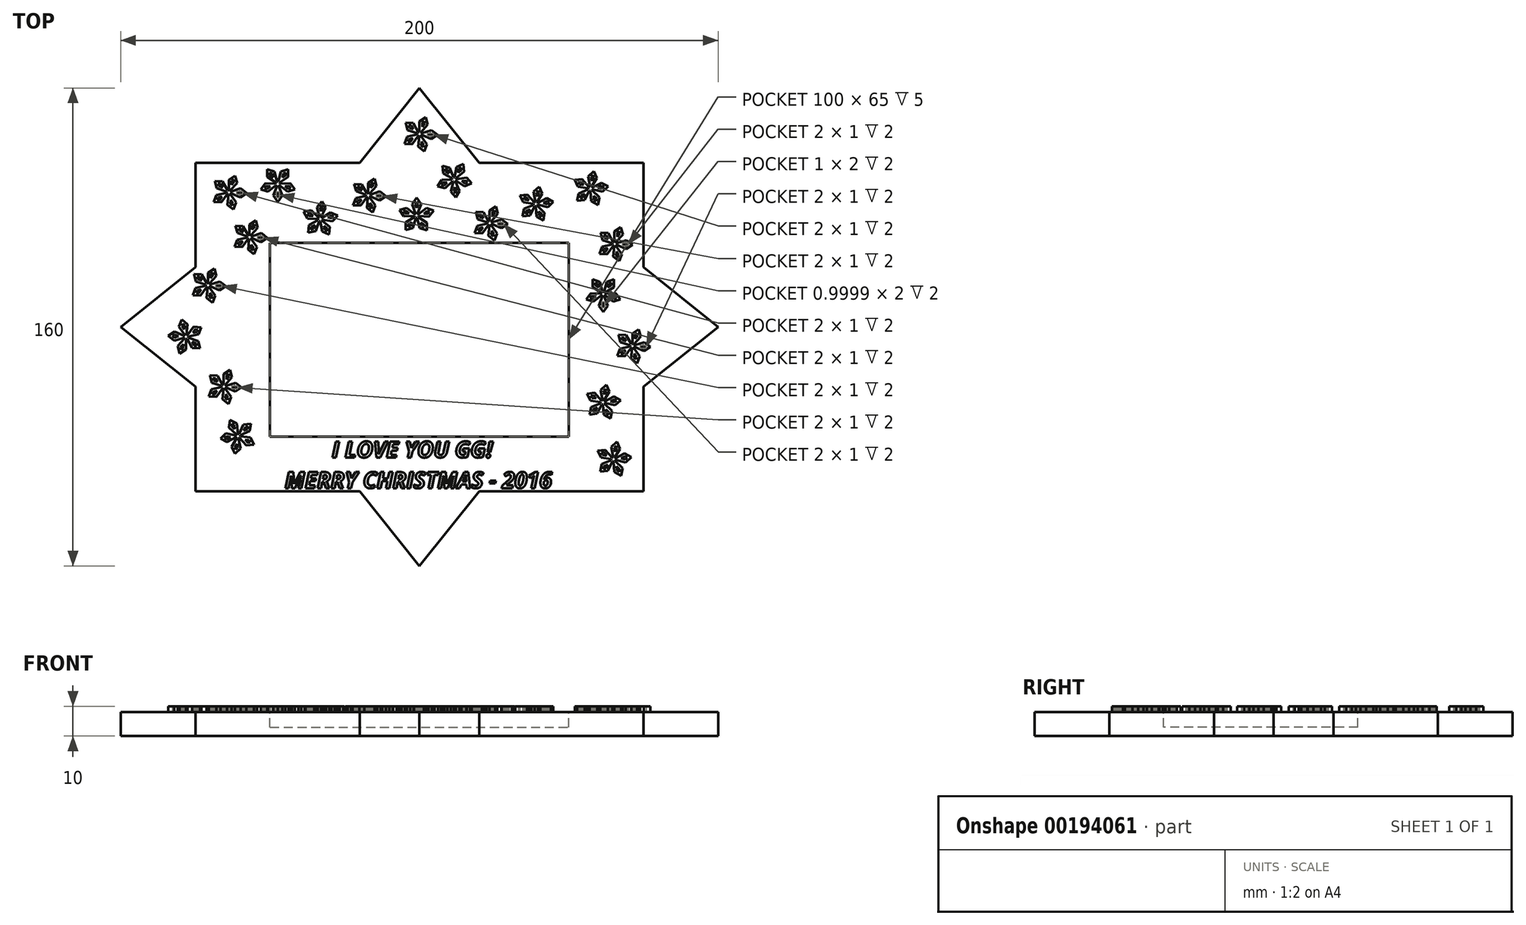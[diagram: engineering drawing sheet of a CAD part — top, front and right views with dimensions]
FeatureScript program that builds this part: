
annotation { "Feature Type Name" : "Feature", "Feature Type Description" : "" }
export const myFeature = defineFeature(function(context is Context, id is Id, definition is map)
    precondition{}
    {
        {
            var Q0;
            Q0=qCreatedBy(makeId("Top.planeOp"),FACE);
            var sketch = newSketch(context, id + "F0", { "sketchPlane" : qUnion([Q0])});
            skLineSegment(sketch, "E0.bottom", {"start": v(75, 55) * mm, "end": v(20, 55) * mm});
            skLineSegment(sketch, "E0.top", {"start": v(75, -55) * mm, "end": v(20, -55) * mm});
            skLineSegment(sketch, "E0.left", {"start": v(75, 55) * mm, "end": v(75, 20) * mm});
            skLineSegment(sketch, "E0.right", {"start": v(-75, 55) * mm, "end": v(-75, 20) * mm});
            skLineSegment(sketch, "E1", {"start": v(75, 20) * mm, "end": v(100, 0) * mm});
            skLineSegment(sketch, "E2", {"start": v(-20, 55) * mm, "end": v(0, 80) * mm});
            skLineSegment(sketch, "E3", {"start": v(0, 80) * mm, "end": v(20, 55) * mm});
            skLineSegment(sketch, "E4.MirrorCS", {"start": v(-20, -55) * mm, "end": v(0, -80) * mm});
            skLineSegment(sketch, "E5.MirrorCS", {"start": v(0, -80) * mm, "end": v(20, -55) * mm});
            skLineSegment(sketch, "E6.MirrorCS", {"start": v(75, -20) * mm, "end": v(100, 0) * mm});
            skLineSegment(sketch, "E7.MirrorCS", {"start": v(-75, 20) * mm, "end": v(-100, 0) * mm});
            skLineSegment(sketch, "E8.MirrorCS", {"start": v(-75, -20) * mm, "end": v(-100, 0) * mm});
            skLineSegment(sketch, "E9.trimOffspring", {"start": v(-75, -20) * mm, "end": v(-75, -55) * mm});
            skLineSegment(sketch, "E10.trimOffspring", {"start": v(75, -20) * mm, "end": v(75, -55) * mm});
            skLineSegment(sketch, "E11.trimOffspring", {"start": v(-20, -55) * mm, "end": v(-75, -55) * mm});
            skLineSegment(sketch, "E12.trimOffspring", {"start": v(-20, 55) * mm, "end": v(-75, 55) * mm});
            skPoint(sketch, "E13.MirrorCS.end.orphan", {"position": v(75, 34.57) * mm});
            skPoint(sketch, "E13.MirrorCS.start.orphan", {"position": v(100, 0) * mm});
            skPoint(sketch, "E14.orphan", {"position": v(75, -34.57) * mm});
            skSolve(sketch);
        }
        {
            var Q0;
            Q0=qSketchRegion(id+"F0",true);
            extrude(context, id + "F1", {"entities" : qUnion([Q0]), "endBound" : BoundingType.SYMMETRIC, "depth" : 8 * mm});
        }
        {
            var Q0;
            Q0=makeQuery(id+"F1.opExtrude","CAP_FACE",FACE,{"disambiguationData":[OSD([sQuery(id+"F0.wireOp",EDGE,"E0.bottom"),sQuery(id+"F0.wireOp",EDGE,"E0.top"),sQuery(id+"F0.wireOp",EDGE,"E0.left"),sQuery(id+"F0.wireOp",EDGE,"E0.right"),sQuery(id+"F0.wireOp",EDGE,"b7ca5f3b-2874-41bd-b902-1c79f96a0a8620.MirrorC"),sQuery(id+"F0.wireOp",EDGE,"b7ca5f3b-2874-41bd-b902-1c79f96a0a8621.MirrorC"),sQuery(id+"F0.wireOp",EDGE,"b7ca5f3b-2874-41bd-b902-1c79f96a0a8622.MirrorCS"),sQuery(id+"F0.wireOp",EDGE,"b7ca5f3b-2874-41bd-b902-1c79f96a0a8623.MirrorCS"),sQuery(id+"F0.wireOp",EDGE,"b7ca5f3b-2874-41bd-b902-1c79f96a0a8624.MirrorCS"),sQuery(id+"F0.wireOp",EDGE,"b7ca5f3b-2874-41bd-b902-1c79f96a0a8625.MirrorCS"),sQuery(id+"F0.wireOp",EDGE,"70034771-ba44-435e-ab74-29499f25fa1546.MirrorC"),sQuery(id+"F0.wireOp",EDGE,"70034771-ba44-435e-ab74-29499f25fa1547.MirrorCS"),sQuery(id+"F0.wireOp",EDGE,"70034771-ba44-435e-ab74-29499f25fa1548.MirrorC"),sQuery(id+"F0.wireOp",EDGE,"70034771-ba44-435e-ab74-29499f25fa1549.MirrorCS"),sQuery(id+"F0.wireOp",EDGE,"70034771-ba44-435e-ab74-29499f25fa1550.MirrorCS"),sQuery(id+"F0.wireOp",EDGE,"70034771-ba44-435e-ab74-29499f25fa1551.MirrorCS"),sQuery(id+"F0.wireOp",EDGE,"E1"),sQuery(id+"F0.wireOp",EDGE,"E2"),sQuery(id+"F0.wireOp",EDGE,"E3"),sQuery(id+"F0.wireOp",EDGE,"E4.MirrorCS"),sQuery(id+"F0.wireOp",EDGE,"E5.MirrorCS"),sQuery(id+"F0.wireOp",EDGE,"E6.MirrorCS"),sQuery(id+"F0.wireOp",EDGE,"E7.MirrorCS"),sQuery(id+"F0.wireOp",EDGE,"E8.MirrorCS"),sQuery(id+"F0.wireOp",EDGE,"E9.trimOffspring"),sQuery(id+"F0.wireOp",EDGE,"E10.trimOffspring"),sQuery(id+"F0.wireOp",EDGE,"E11.trimOffspring"),sQuery(id+"F0.wireOp",EDGE,"E12.trimOffspring")])],"isStart":false});
            var sketch = newSketch(context, id + "F2", { "sketchPlane" : qUnion([Q0])});
            skCircle(sketch, "E15.cCircle", {"center": v(65.31, 27.78) * mm, "radius": 6 * mm, "construction": true});
            skLineSegment(sketch, "E15.0", {"start": v(71.3, 27.48) * mm, "end": v(66.88, 22) * mm, "construction": true});
            skLineSegment(sketch, "E15.1", {"start": v(66.88, 22) * mm, "end": v(60.29, 24.5) * mm, "construction": true});
            skLineSegment(sketch, "E15.2", {"start": v(60.29, 24.5) * mm, "end": v(60.64, 31.55) * mm, "construction": true});
            skLineSegment(sketch, "E15.3", {"start": v(60.64, 31.55) * mm, "end": v(67.45, 33.39) * mm, "construction": true});
            skLineSegment(sketch, "E15.4", {"start": v(67.45, 33.39) * mm, "end": v(71.3, 27.48) * mm, "construction": true});
            skLineSegment(sketch, "E16", {"start": v(60.64, 31.55) * mm, "end": v(61.32, 29.08) * mm});
            skLineSegment(sketch, "E17", {"start": v(61.32, 29.08) * mm, "end": v(64.6, 28.02) * mm});
            skLineSegment(sketch, "E18", {"start": v(64.94, 28.43) * mm, "end": v(63.2, 31.42) * mm});
            skLineSegment(sketch, "E19", {"start": v(63.2, 31.42) * mm, "end": v(60.64, 31.55) * mm});
            skLineSegment(sketch, "E20", {"start": v(60.29, 24.5) * mm, "end": v(62.84, 24.38) * mm});
            skLineSegment(sketch, "E21", {"start": v(62.84, 24.38) * mm, "end": v(64.87, 27.18) * mm});
            skLineSegment(sketch, "E22", {"start": v(64.58, 27.63) * mm, "end": v(61.2, 26.9) * mm});
            skLineSegment(sketch, "E23", {"start": v(61.2, 26.9) * mm, "end": v(60.29, 24.5) * mm});
            skLineSegment(sketch, "E24", {"start": v(66.88, 22) * mm, "end": v(67.78, 24.38) * mm});
            skLineSegment(sketch, "E25", {"start": v(67.78, 24.38) * mm, "end": v(65.75, 27.18) * mm});
            skLineSegment(sketch, "E26", {"start": v(65.24, 27.04) * mm, "end": v(64.89, 23.6) * mm});
            skLineSegment(sketch, "E27", {"start": v(64.89, 23.6) * mm, "end": v(66.88, 22) * mm});
            skLineSegment(sketch, "E28", {"start": v(66, 27.48) * mm, "end": v(69.16, 26.09) * mm});
            skLineSegment(sketch, "E29", {"start": v(69.16, 26.09) * mm, "end": v(71.3, 27.48) * mm});
            skLineSegment(sketch, "E30", {"start": v(66.03, 28.02) * mm, "end": v(69.31, 29.08) * mm});
            skLineSegment(sketch, "E31", {"start": v(69.31, 29.08) * mm, "end": v(71.3, 27.48) * mm});
            skLineSegment(sketch, "E32", {"start": v(67.45, 33.39) * mm, "end": v(68.12, 30.92) * mm});
            skLineSegment(sketch, "E33", {"start": v(68.12, 30.92) * mm, "end": v(65.81, 28.34) * mm});
            skLineSegment(sketch, "E34", {"start": v(65.31, 28.53) * mm, "end": v(65.31, 31.99) * mm});
            skLineSegment(sketch, "E35", {"start": v(65.31, 31.99) * mm, "end": v(67.45, 33.39) * mm});
            skLineSegment(sketch, "E36", {"start": v(69.38, 30.43) * mm, "end": v(69.1, 24.74) * mm, "construction": true});
            skLineSegment(sketch, "E37", {"start": v(69.1, 24.74) * mm, "end": v(63.58, 23.25) * mm, "construction": true});
            skLineSegment(sketch, "E38", {"start": v(63.58, 23.25) * mm, "end": v(60.47, 28.03) * mm, "construction": true});
            skLineSegment(sketch, "E39", {"start": v(60.47, 28.03) * mm, "end": v(64.05, 32.47) * mm, "construction": true});
            skLineSegment(sketch, "E40", {"start": v(64.05, 32.47) * mm, "end": v(69.38, 30.43) * mm, "construction": true});
            skLineSegment(sketch, "E41", {"start": v(67.45, 33.39) * mm, "end": v(65.31, 27.78) * mm, "construction": true});
            skLineSegment(sketch, "E42", {"start": v(71.3, 27.48) * mm, "end": v(65.31, 27.78) * mm, "construction": true});
            skLineSegment(sketch, "E43", {"start": v(66.88, 22) * mm, "end": v(65.31, 27.78) * mm, "construction": true});
            skLineSegment(sketch, "E44", {"start": v(60.29, 24.5) * mm, "end": v(65.31, 27.78) * mm, "construction": true});
            skLineSegment(sketch, "E45", {"start": v(60.64, 31.55) * mm, "end": v(65.31, 27.78) * mm, "construction": true});
            skArc(sketch, "E46", {"start": v(64.87, 27.18) * mm, "mid": v(65.05, 27.08) * mm, "end": v(65.24, 27.04) * mm});
            skArc(sketch, "E47.trimOffspring", {"start": v(64.6, 28.02) * mm, "mid": v(64.56, 27.82) * mm, "end": v(64.58, 27.63) * mm});
            skArc(sketch, "E48.trimOffspring", {"start": v(65.31, 28.53) * mm, "mid": v(65.12, 28.5) * mm, "end": v(64.94, 28.43) * mm});
            skArc(sketch, "E49.trimOffspring", {"start": v(66.03, 28.02) * mm, "mid": v(65.94, 28.2) * mm, "end": v(65.81, 28.34) * mm});
            skArc(sketch, "E50.trimOffspring", {"start": v(65.75, 27.18) * mm, "mid": v(65.9, 27.31) * mm, "end": v(66, 27.48) * mm});
            skLineSegment(sketch, "E51", {"start": v(61.72, 30.68) * mm, "end": v(61.94, 29.86) * mm});
            skLineSegment(sketch, "E52", {"start": v(61.94, 29.86) * mm, "end": v(63.28, 29.43) * mm});
            skLineSegment(sketch, "E53", {"start": v(63.28, 29.43) * mm, "end": v(62.57, 30.64) * mm});
            skLineSegment(sketch, "E54", {"start": v(62.57, 30.64) * mm, "end": v(61.72, 30.68) * mm});
            skLineSegment(sketch, "E55", {"start": v(66.96, 32.1) * mm, "end": v(67.18, 31.27) * mm});
            skLineSegment(sketch, "E56", {"start": v(67.18, 31.27) * mm, "end": v(66.25, 30.23) * mm});
            skLineSegment(sketch, "E57", {"start": v(66.25, 30.23) * mm, "end": v(66.25, 31.63) * mm});
            skLineSegment(sketch, "E58", {"start": v(66.25, 31.63) * mm, "end": v(66.96, 32.1) * mm});
            skLineSegment(sketch, "E59", {"start": v(66.52, 23.33) * mm, "end": v(66.82, 24.12) * mm});
            skLineSegment(sketch, "E60", {"start": v(66.82, 24.12) * mm, "end": v(66, 25.26) * mm});
            skLineSegment(sketch, "E61", {"start": v(66, 25.26) * mm, "end": v(65.85, 23.86) * mm});
            skLineSegment(sketch, "E62", {"start": v(65.85, 23.86) * mm, "end": v(66.52, 23.33) * mm});
            skLineSegment(sketch, "E63", {"start": v(69.93, 27.55) * mm, "end": v(69.26, 28.09) * mm});
            skLineSegment(sketch, "E64", {"start": v(69.26, 28.09) * mm, "end": v(67.93, 27.65) * mm});
            skLineSegment(sketch, "E65", {"start": v(67.93, 27.65) * mm, "end": v(69.21, 27.09) * mm});
            skLineSegment(sketch, "E66", {"start": v(69.21, 27.09) * mm, "end": v(69.93, 27.55) * mm});
            skLineSegment(sketch, "E67", {"start": v(61.44, 25.26) * mm, "end": v(62.3, 25.22) * mm});
            skLineSegment(sketch, "E68", {"start": v(62.3, 25.22) * mm, "end": v(63.12, 26.35) * mm});
            skLineSegment(sketch, "E69", {"start": v(63.12, 26.35) * mm, "end": v(61.75, 26.06) * mm});
            skLineSegment(sketch, "E70", {"start": v(61.75, 26.06) * mm, "end": v(61.44, 25.26) * mm});
            skLineSegment(sketch, "E71", {"start": v(58.04, 15.9) * mm, "end": v(58.05, 13.34) * mm});
            skLineSegment(sketch, "E72", {"start": v(58.05, 13.34) * mm, "end": v(60.95, 11.46) * mm});
            skLineSegment(sketch, "E73", {"start": v(61.38, 11.77) * mm, "end": v(60.47, 15.1) * mm});
            skLineSegment(sketch, "E74", {"start": v(60.47, 15.1) * mm, "end": v(58.04, 15.9) * mm});
            skLineSegment(sketch, "E75", {"start": v(55.87, 9.19) * mm, "end": v(58.3, 8.4) * mm});
            skLineSegment(sketch, "E76", {"start": v(58.3, 8.4) * mm, "end": v(61, 10.58) * mm});
            skLineSegment(sketch, "E77", {"start": v(60.83, 11.09) * mm, "end": v(57.38, 11.26) * mm});
            skLineSegment(sketch, "E78", {"start": v(57.38, 11.26) * mm, "end": v(55.87, 9.19) * mm});
            skLineSegment(sketch, "E79", {"start": v(61.59, 5.05) * mm, "end": v(63.08, 7.13) * mm});
            skLineSegment(sketch, "E80", {"start": v(63.08, 7.13) * mm, "end": v(61.84, 10.35) * mm});
            skLineSegment(sketch, "E81", {"start": v(61.3, 10.35) * mm, "end": v(60.08, 7.12) * mm});
            skLineSegment(sketch, "E82", {"start": v(60.08, 7.12) * mm, "end": v(61.59, 5.05) * mm});
            skLineSegment(sketch, "E83", {"start": v(62.16, 10.58) * mm, "end": v(64.85, 8.42) * mm});
            skLineSegment(sketch, "E84", {"start": v(64.85, 8.42) * mm, "end": v(67.29, 9.2) * mm});
            skLineSegment(sketch, "E85", {"start": v(62.32, 11.09) * mm, "end": v(65.77, 11.27) * mm});
            skLineSegment(sketch, "E86", {"start": v(65.77, 11.27) * mm, "end": v(67.29, 9.2) * mm});
            skLineSegment(sketch, "E87", {"start": v(65.1, 15.9) * mm, "end": v(65.1, 13.35) * mm});
            skLineSegment(sketch, "E88", {"start": v(65.1, 13.35) * mm, "end": v(62.2, 11.46) * mm});
            skLineSegment(sketch, "E89", {"start": v(61.77, 11.77) * mm, "end": v(62.66, 15.11) * mm});
            skLineSegment(sketch, "E90", {"start": v(62.66, 15.11) * mm, "end": v(65.1, 15.9) * mm});
            skArc(sketch, "E91", {"start": v(61, 10.58) * mm, "mid": v(61.14, 10.44) * mm, "end": v(61.3, 10.35) * mm});
            skArc(sketch, "E92.trimOffspring", {"start": v(60.95, 11.46) * mm, "mid": v(60.86, 11.28) * mm, "end": v(60.83, 11.09) * mm});
            skArc(sketch, "E93.trimOffspring", {"start": v(61.77, 11.77) * mm, "mid": v(61.57, 11.8) * mm, "end": v(61.38, 11.77) * mm});
            skArc(sketch, "E94.trimOffspring", {"start": v(62.32, 11.09) * mm, "mid": v(62.29, 11.28) * mm, "end": v(62.2, 11.46) * mm});
            skArc(sketch, "E95.trimOffspring", {"start": v(61.84, 10.35) * mm, "mid": v(62.02, 10.44) * mm, "end": v(62.16, 10.58) * mm});
            skLineSegment(sketch, "E96", {"start": v(58.86, 14.78) * mm, "end": v(58.86, 13.93) * mm});
            skLineSegment(sketch, "E97", {"start": v(58.86, 13.93) * mm, "end": v(60.03, 13.17) * mm});
            skLineSegment(sketch, "E98", {"start": v(60.03, 13.17) * mm, "end": v(59.67, 14.52) * mm});
            skLineSegment(sketch, "E99", {"start": v(59.67, 14.52) * mm, "end": v(58.86, 14.78) * mm});
            skLineSegment(sketch, "E100", {"start": v(64.28, 14.8) * mm, "end": v(64.28, 13.94) * mm});
            skLineSegment(sketch, "E101", {"start": v(64.28, 13.94) * mm, "end": v(63.11, 13.17) * mm});
            skLineSegment(sketch, "E102", {"start": v(63.11, 13.17) * mm, "end": v(63.47, 14.52) * mm});
            skLineSegment(sketch, "E103", {"start": v(63.47, 14.52) * mm, "end": v(64.28, 14.8) * mm});
            skLineSegment(sketch, "E104", {"start": v(61.58, 6.43) * mm, "end": v(62.08, 7.12) * mm});
            skLineSegment(sketch, "E105", {"start": v(62.08, 7.12) * mm, "end": v(61.58, 8.43) * mm});
            skLineSegment(sketch, "E106", {"start": v(61.58, 8.43) * mm, "end": v(61.08, 7.12) * mm});
            skLineSegment(sketch, "E107", {"start": v(61.08, 7.12) * mm, "end": v(61.58, 6.43) * mm});
            skLineSegment(sketch, "E108", {"start": v(65.97, 9.63) * mm, "end": v(65.47, 10.32) * mm});
            skLineSegment(sketch, "E109", {"start": v(65.47, 10.32) * mm, "end": v(64.07, 10.25) * mm});
            skLineSegment(sketch, "E110", {"start": v(64.07, 10.25) * mm, "end": v(65.16, 9.37) * mm});
            skLineSegment(sketch, "E111", {"start": v(65.16, 9.37) * mm, "end": v(65.97, 9.63) * mm});
            skLineSegment(sketch, "E112", {"start": v(57.19, 9.62) * mm, "end": v(58, 9.35) * mm});
            skLineSegment(sketch, "E113", {"start": v(58, 9.35) * mm, "end": v(59.09, 10.24) * mm});
            skLineSegment(sketch, "E114", {"start": v(59.09, 10.24) * mm, "end": v(57.69, 10.3) * mm});
            skLineSegment(sketch, "E115", {"start": v(57.69, 10.3) * mm, "end": v(57.19, 9.62) * mm});
            skLineSegment(sketch, "E116", {"start": v(52, 49.2) * mm, "end": v(53.08, 46.88) * mm});
            skLineSegment(sketch, "E117", {"start": v(53.08, 46.88) * mm, "end": v(56.5, 46.4) * mm});
            skLineSegment(sketch, "E118", {"start": v(56.76, 46.87) * mm, "end": v(54.53, 49.5) * mm});
            skLineSegment(sketch, "E119", {"start": v(54.53, 49.5) * mm, "end": v(52, 49.2) * mm});
            skLineSegment(sketch, "E120", {"start": v(52.86, 42.2) * mm, "end": v(55.4, 42.52) * mm});
            skLineSegment(sketch, "E121", {"start": v(55.4, 42.52) * mm, "end": v(56.92, 45.62) * mm});
            skLineSegment(sketch, "E122", {"start": v(56.55, 46.01) * mm, "end": v(53.35, 44.7) * mm});
            skLineSegment(sketch, "E123", {"start": v(53.35, 44.7) * mm, "end": v(52.86, 42.2) * mm});
            skLineSegment(sketch, "E124", {"start": v(59.79, 40.86) * mm, "end": v(60.27, 43.37) * mm});
            skLineSegment(sketch, "E125", {"start": v(60.27, 43.37) * mm, "end": v(57.78, 45.77) * mm});
            skLineSegment(sketch, "E126", {"start": v(57.3, 45.55) * mm, "end": v(57.55, 42.1) * mm});
            skLineSegment(sketch, "E127", {"start": v(57.55, 42.1) * mm, "end": v(59.79, 40.86) * mm});
            skLineSegment(sketch, "E128", {"start": v(57.97, 46.12) * mm, "end": v(61.33, 45.3) * mm});
            skLineSegment(sketch, "E129", {"start": v(61.33, 45.3) * mm, "end": v(63.2, 47.04) * mm});
            skLineSegment(sketch, "E130", {"start": v(57.9, 46.65) * mm, "end": v(60.96, 48.27) * mm});
            skLineSegment(sketch, "E131", {"start": v(60.96, 48.27) * mm, "end": v(63.2, 47.04) * mm});
            skLineSegment(sketch, "E132", {"start": v(58.38, 52.19) * mm, "end": v(59.46, 49.87) * mm});
            skLineSegment(sketch, "E133", {"start": v(59.46, 49.87) * mm, "end": v(57.64, 46.93) * mm});
            skLineSegment(sketch, "E134", {"start": v(57.11, 47.03) * mm, "end": v(56.51, 50.43) * mm});
            skLineSegment(sketch, "E135", {"start": v(56.51, 50.43) * mm, "end": v(58.38, 52.19) * mm});
            skArc(sketch, "E136", {"start": v(56.92, 45.62) * mm, "mid": v(57.1, 45.56) * mm, "end": v(57.3, 45.55) * mm});
            skArc(sketch, "E137.trimOffspring", {"start": v(56.5, 46.4) * mm, "mid": v(56.5, 46.2) * mm, "end": v(56.55, 46.01) * mm});
            skArc(sketch, "E138.trimOffspring", {"start": v(57.11, 47.03) * mm, "mid": v(56.93, 46.97) * mm, "end": v(56.76, 46.87) * mm});
            skArc(sketch, "E139.trimOffspring", {"start": v(57.9, 46.65) * mm, "mid": v(57.8, 46.8) * mm, "end": v(57.64, 46.93) * mm});
            skArc(sketch, "E140.trimOffspring", {"start": v(57.78, 45.77) * mm, "mid": v(57.9, 45.93) * mm, "end": v(57.97, 46.12) * mm});
            skLineSegment(sketch, "E141", {"start": v(53.2, 48.53) * mm, "end": v(53.56, 47.76) * mm});
            skLineSegment(sketch, "E142", {"start": v(53.56, 47.76) * mm, "end": v(54.95, 47.56) * mm});
            skLineSegment(sketch, "E143", {"start": v(54.95, 47.56) * mm, "end": v(54.05, 48.63) * mm});
            skLineSegment(sketch, "E144", {"start": v(54.05, 48.63) * mm, "end": v(53.2, 48.53) * mm});
            skLineSegment(sketch, "E145", {"start": v(58.12, 50.83) * mm, "end": v(58.48, 50.06) * mm});
            skLineSegment(sketch, "E146", {"start": v(58.48, 50.06) * mm, "end": v(57.74, 48.87) * mm});
            skLineSegment(sketch, "E147", {"start": v(57.74, 48.87) * mm, "end": v(57.5, 50.25) * mm});
            skLineSegment(sketch, "E148", {"start": v(57.5, 50.25) * mm, "end": v(58.12, 50.83) * mm});
            skLineSegment(sketch, "E149", {"start": v(59.2, 42.11) * mm, "end": v(59.36, 42.95) * mm});
            skLineSegment(sketch, "E150", {"start": v(59.36, 42.95) * mm, "end": v(58.35, 43.92) * mm});
            skLineSegment(sketch, "E151", {"start": v(58.35, 43.92) * mm, "end": v(58.46, 42.53) * mm});
            skLineSegment(sketch, "E152", {"start": v(58.46, 42.53) * mm, "end": v(59.2, 42.11) * mm});
            skLineSegment(sketch, "E153", {"start": v(61.83, 46.87) * mm, "end": v(61.08, 47.28) * mm});
            skLineSegment(sketch, "E154", {"start": v(61.08, 47.28) * mm, "end": v(59.84, 46.62) * mm});
            skLineSegment(sketch, "E155", {"start": v(59.84, 46.62) * mm, "end": v(61.2, 46.28) * mm});
            skLineSegment(sketch, "E156", {"start": v(61.2, 46.28) * mm, "end": v(61.83, 46.87) * mm});
            skLineSegment(sketch, "E157", {"start": v(53.87, 43.14) * mm, "end": v(54.72, 43.25) * mm});
            skLineSegment(sketch, "E158", {"start": v(54.72, 43.25) * mm, "end": v(55.33, 44.5) * mm});
            skLineSegment(sketch, "E159", {"start": v(55.33, 44.5) * mm, "end": v(54.04, 43.98) * mm});
            skLineSegment(sketch, "E160", {"start": v(54.04, 43.98) * mm, "end": v(53.87, 43.14) * mm});
            skLineSegment(sketch, "E161", {"start": v(66.62, -2.64) * mm, "end": v(67.3, -5.1) * mm});
            skLineSegment(sketch, "E162", {"start": v(67.3, -5.1) * mm, "end": v(70.58, -6.18) * mm});
            skLineSegment(sketch, "E163", {"start": v(70.91, -5.76) * mm, "end": v(69.18, -2.77) * mm});
            skLineSegment(sketch, "E164", {"start": v(69.18, -2.77) * mm, "end": v(66.62, -2.64) * mm});
            skLineSegment(sketch, "E165", {"start": v(66.26, -9.68) * mm, "end": v(68.82, -9.8) * mm});
            skLineSegment(sketch, "E166", {"start": v(68.82, -9.8) * mm, "end": v(70.85, -7.02) * mm});
            skLineSegment(sketch, "E167", {"start": v(70.56, -6.57) * mm, "end": v(67.18, -7.3) * mm});
            skLineSegment(sketch, "E168", {"start": v(67.18, -7.3) * mm, "end": v(66.26, -9.68) * mm});
            skLineSegment(sketch, "E169", {"start": v(72.85, -12.2) * mm, "end": v(73.76, -9.8) * mm});
            skLineSegment(sketch, "E170", {"start": v(73.76, -9.8) * mm, "end": v(71.73, -7.02) * mm});
            skLineSegment(sketch, "E171", {"start": v(71.21, -7.15) * mm, "end": v(70.86, -10.6) * mm});
            skLineSegment(sketch, "E172", {"start": v(70.86, -10.6) * mm, "end": v(72.85, -12.2) * mm});
            skLineSegment(sketch, "E173", {"start": v(71.98, -6.71) * mm, "end": v(75.14, -8.1) * mm});
            skLineSegment(sketch, "E174", {"start": v(75.14, -8.1) * mm, "end": v(77.28, -6.71) * mm});
            skLineSegment(sketch, "E175", {"start": v(72, -6.18) * mm, "end": v(75.29, -5.1) * mm});
            skLineSegment(sketch, "E176", {"start": v(75.29, -5.1) * mm, "end": v(77.28, -6.71) * mm});
            skLineSegment(sketch, "E177", {"start": v(73.43, -0.8) * mm, "end": v(74.1, -3.28) * mm});
            skLineSegment(sketch, "E178", {"start": v(74.1, -3.28) * mm, "end": v(71.8, -5.85) * mm});
            skLineSegment(sketch, "E179", {"start": v(71.3, -5.66) * mm, "end": v(71.3, -2.2) * mm});
            skLineSegment(sketch, "E180", {"start": v(71.3, -2.2) * mm, "end": v(73.43, -0.8) * mm});
            skArc(sketch, "E181", {"start": v(70.85, -7.02) * mm, "mid": v(71.02, -7.1) * mm, "end": v(71.21, -7.15) * mm});
            skArc(sketch, "E182.trimOffspring", {"start": v(70.58, -6.18) * mm, "mid": v(70.54, -6.37) * mm, "end": v(70.56, -6.57) * mm});
            skArc(sketch, "E183.trimOffspring", {"start": v(71.3, -5.66) * mm, "mid": v(71.1, -5.68) * mm, "end": v(70.91, -5.76) * mm});
            skArc(sketch, "E184.trimOffspring", {"start": v(72, -6.18) * mm, "mid": v(71.92, -6) * mm, "end": v(71.8, -5.85) * mm});
            skArc(sketch, "E185.trimOffspring", {"start": v(71.73, -7.02) * mm, "mid": v(71.87, -6.88) * mm, "end": v(71.98, -6.71) * mm});
            skLineSegment(sketch, "E186", {"start": v(67.7, -3.5) * mm, "end": v(67.92, -4.33) * mm});
            skLineSegment(sketch, "E187", {"start": v(67.92, -4.33) * mm, "end": v(69.25, -4.76) * mm});
            skLineSegment(sketch, "E188", {"start": v(69.25, -4.76) * mm, "end": v(68.55, -3.55) * mm});
            skLineSegment(sketch, "E189", {"start": v(68.55, -3.55) * mm, "end": v(67.7, -3.5) * mm});
            skLineSegment(sketch, "E190", {"start": v(72.94, -2.1) * mm, "end": v(73.16, -2.92) * mm});
            skLineSegment(sketch, "E191", {"start": v(73.16, -2.92) * mm, "end": v(72.22, -3.96) * mm});
            skLineSegment(sketch, "E192", {"start": v(72.22, -3.96) * mm, "end": v(72.22, -2.56) * mm});
            skLineSegment(sketch, "E193", {"start": v(72.22, -2.56) * mm, "end": v(72.94, -2.1) * mm});
            skLineSegment(sketch, "E194", {"start": v(72.5, -10.87) * mm, "end": v(72.8, -10.07) * mm});
            skLineSegment(sketch, "E195", {"start": v(72.8, -10.07) * mm, "end": v(71.97, -8.94) * mm});
            skLineSegment(sketch, "E196", {"start": v(71.97, -8.94) * mm, "end": v(71.83, -10.33) * mm});
            skLineSegment(sketch, "E197", {"start": v(71.83, -10.33) * mm, "end": v(72.5, -10.87) * mm});
            skLineSegment(sketch, "E198", {"start": v(75.9, -6.64) * mm, "end": v(75.24, -6.1) * mm});
            skLineSegment(sketch, "E199", {"start": v(75.24, -6.1) * mm, "end": v(73.9, -6.54) * mm});
            skLineSegment(sketch, "E200", {"start": v(73.9, -6.54) * mm, "end": v(75.19, -7.1) * mm});
            skLineSegment(sketch, "E201", {"start": v(75.19, -7.1) * mm, "end": v(75.9, -6.64) * mm});
            skLineSegment(sketch, "E202", {"start": v(67.42, -8.93) * mm, "end": v(68.27, -8.97) * mm});
            skLineSegment(sketch, "E203", {"start": v(68.27, -8.97) * mm, "end": v(69.1, -7.84) * mm});
            skLineSegment(sketch, "E204", {"start": v(69.1, -7.84) * mm, "end": v(67.73, -8.13) * mm});
            skLineSegment(sketch, "E205", {"start": v(67.73, -8.13) * mm, "end": v(67.42, -8.93) * mm});
            skLineSegment(sketch, "E206", {"start": v(56.16, -22.34) * mm, "end": v(57.25, -24.66) * mm});
            skLineSegment(sketch, "E207", {"start": v(57.25, -24.66) * mm, "end": v(60.67, -25.14) * mm});
            skLineSegment(sketch, "E208", {"start": v(60.93, -24.67) * mm, "end": v(58.7, -22.03) * mm});
            skLineSegment(sketch, "E209", {"start": v(58.7, -22.03) * mm, "end": v(56.16, -22.34) * mm});
            skLineSegment(sketch, "E210", {"start": v(57.03, -29.34) * mm, "end": v(59.57, -29.02) * mm});
            skLineSegment(sketch, "E211", {"start": v(59.57, -29.02) * mm, "end": v(61.09, -25.92) * mm});
            skLineSegment(sketch, "E212", {"start": v(60.72, -25.53) * mm, "end": v(57.52, -26.83) * mm});
            skLineSegment(sketch, "E213", {"start": v(57.52, -26.83) * mm, "end": v(57.03, -29.34) * mm});
            skLineSegment(sketch, "E214", {"start": v(63.96, -30.68) * mm, "end": v(64.44, -28.16) * mm});
            skLineSegment(sketch, "E215", {"start": v(64.44, -28.16) * mm, "end": v(61.95, -25.76) * mm});
            skLineSegment(sketch, "E216", {"start": v(61.47, -26) * mm, "end": v(61.72, -29.44) * mm});
            skLineSegment(sketch, "E217", {"start": v(61.72, -29.44) * mm, "end": v(63.96, -30.68) * mm});
            skLineSegment(sketch, "E218", {"start": v(62.14, -25.42) * mm, "end": v(65.5, -26.25) * mm});
            skLineSegment(sketch, "E219", {"start": v(65.5, -26.25) * mm, "end": v(67.37, -24.5) * mm});
            skLineSegment(sketch, "E220", {"start": v(62.08, -24.9) * mm, "end": v(65.13, -23.27) * mm});
            skLineSegment(sketch, "E221", {"start": v(65.13, -23.27) * mm, "end": v(67.37, -24.5) * mm});
            skLineSegment(sketch, "E222", {"start": v(62.55, -19.35) * mm, "end": v(63.63, -21.67) * mm});
            skLineSegment(sketch, "E223", {"start": v(63.63, -21.67) * mm, "end": v(61.81, -24.6) * mm});
            skLineSegment(sketch, "E224", {"start": v(61.28, -24.5) * mm, "end": v(60.68, -21.1) * mm});
            skLineSegment(sketch, "E225", {"start": v(60.68, -21.1) * mm, "end": v(62.55, -19.35) * mm});
            skArc(sketch, "E226", {"start": v(61.09, -25.92) * mm, "mid": v(61.27, -25.98) * mm, "end": v(61.47, -26) * mm});
            skArc(sketch, "E227.trimOffspring", {"start": v(60.67, -25.14) * mm, "mid": v(60.67, -25.34) * mm, "end": v(60.72, -25.53) * mm});
            skArc(sketch, "E228.trimOffspring", {"start": v(61.28, -24.5) * mm, "mid": v(61.1, -24.56) * mm, "end": v(60.93, -24.67) * mm});
            skArc(sketch, "E229.trimOffspring", {"start": v(62.08, -24.9) * mm, "mid": v(61.96, -24.73) * mm, "end": v(61.81, -24.6) * mm});
            skArc(sketch, "E230.trimOffspring", {"start": v(61.95, -25.76) * mm, "mid": v(62.07, -25.6) * mm, "end": v(62.14, -25.42) * mm});
            skLineSegment(sketch, "E231", {"start": v(57.37, -23.01) * mm, "end": v(57.74, -23.78) * mm});
            skLineSegment(sketch, "E232", {"start": v(57.74, -23.78) * mm, "end": v(59.12, -23.98) * mm});
            skLineSegment(sketch, "E233", {"start": v(59.12, -23.98) * mm, "end": v(58.22, -22.9) * mm});
            skLineSegment(sketch, "E234", {"start": v(58.22, -22.9) * mm, "end": v(57.37, -23.01) * mm});
            skLineSegment(sketch, "E235", {"start": v(62.29, -20.7) * mm, "end": v(62.65, -21.48) * mm});
            skLineSegment(sketch, "E236", {"start": v(62.65, -21.48) * mm, "end": v(61.91, -22.67) * mm});
            skLineSegment(sketch, "E237", {"start": v(61.91, -22.67) * mm, "end": v(61.67, -21.3) * mm});
            skLineSegment(sketch, "E238", {"start": v(61.67, -21.3) * mm, "end": v(62.29, -20.7) * mm});
            skLineSegment(sketch, "E239", {"start": v(63.37, -29.42) * mm, "end": v(63.53, -28.59) * mm});
            skLineSegment(sketch, "E240", {"start": v(63.53, -28.59) * mm, "end": v(62.53, -27.61) * mm});
            skLineSegment(sketch, "E241", {"start": v(62.53, -27.61) * mm, "end": v(62.63, -29.01) * mm});
            skLineSegment(sketch, "E242", {"start": v(62.63, -29.01) * mm, "end": v(63.37, -29.42) * mm});
            skLineSegment(sketch, "E243", {"start": v(66, -24.67) * mm, "end": v(65.25, -24.26) * mm});
            skLineSegment(sketch, "E244", {"start": v(65.25, -24.26) * mm, "end": v(64.01, -24.92) * mm});
            skLineSegment(sketch, "E245", {"start": v(64.01, -24.92) * mm, "end": v(65.37, -25.25) * mm});
            skLineSegment(sketch, "E246", {"start": v(65.37, -25.25) * mm, "end": v(66, -24.67) * mm});
            skLineSegment(sketch, "E247", {"start": v(58.04, -28.4) * mm, "end": v(58.89, -28.3) * mm});
            skLineSegment(sketch, "E248", {"start": v(58.89, -28.3) * mm, "end": v(59.5, -27.03) * mm});
            skLineSegment(sketch, "E249", {"start": v(59.5, -27.03) * mm, "end": v(58.2, -27.56) * mm});
            skLineSegment(sketch, "E250", {"start": v(58.2, -27.56) * mm, "end": v(58.04, -28.4) * mm});
            skLineSegment(sketch, "E251", {"start": v(59.72, -41.45) * mm, "end": v(60.8, -43.76) * mm});
            skLineSegment(sketch, "E252", {"start": v(60.8, -43.76) * mm, "end": v(64.23, -44.24) * mm});
            skLineSegment(sketch, "E253", {"start": v(64.48, -43.77) * mm, "end": v(62.26, -41.13) * mm});
            skLineSegment(sketch, "E254", {"start": v(62.26, -41.13) * mm, "end": v(59.72, -41.45) * mm});
            skLineSegment(sketch, "E255", {"start": v(60.59, -48.44) * mm, "end": v(63.13, -48.12) * mm});
            skLineSegment(sketch, "E256", {"start": v(63.13, -48.12) * mm, "end": v(64.64, -45.02) * mm});
            skLineSegment(sketch, "E257", {"start": v(64.27, -44.63) * mm, "end": v(61.08, -45.93) * mm});
            skLineSegment(sketch, "E258", {"start": v(61.08, -45.93) * mm, "end": v(60.59, -48.44) * mm});
            skLineSegment(sketch, "E259", {"start": v(67.51, -49.78) * mm, "end": v(68, -47.27) * mm});
            skLineSegment(sketch, "E260", {"start": v(68, -47.27) * mm, "end": v(65.5, -44.87) * mm});
            skLineSegment(sketch, "E261", {"start": v(65.02, -45.1) * mm, "end": v(65.28, -48.54) * mm});
            skLineSegment(sketch, "E262", {"start": v(65.28, -48.54) * mm, "end": v(67.51, -49.78) * mm});
            skLineSegment(sketch, "E263", {"start": v(65.7, -44.52) * mm, "end": v(69.05, -45.35) * mm});
            skLineSegment(sketch, "E264", {"start": v(69.05, -45.35) * mm, "end": v(70.92, -43.6) * mm});
            skLineSegment(sketch, "E265", {"start": v(65.63, -44) * mm, "end": v(68.68, -42.37) * mm});
            skLineSegment(sketch, "E266", {"start": v(68.68, -42.37) * mm, "end": v(70.92, -43.6) * mm});
            skLineSegment(sketch, "E267", {"start": v(66.1, -38.45) * mm, "end": v(67.18, -40.77) * mm});
            skLineSegment(sketch, "E268", {"start": v(67.18, -40.77) * mm, "end": v(65.36, -43.7) * mm});
            skLineSegment(sketch, "E269", {"start": v(64.84, -43.6) * mm, "end": v(64.24, -40.2) * mm});
            skLineSegment(sketch, "E270", {"start": v(64.24, -40.2) * mm, "end": v(66.1, -38.45) * mm});
            skArc(sketch, "E271", {"start": v(64.64, -45.02) * mm, "mid": v(64.83, -45.08) * mm, "end": v(65.02, -45.1) * mm});
            skArc(sketch, "E272.trimOffspring", {"start": v(64.23, -44.24) * mm, "mid": v(64.22, -44.44) * mm, "end": v(64.27, -44.63) * mm});
            skArc(sketch, "E273.trimOffspring", {"start": v(64.84, -43.6) * mm, "mid": v(64.65, -43.67) * mm, "end": v(64.48, -43.77) * mm});
            skArc(sketch, "E274.trimOffspring", {"start": v(65.63, -44) * mm, "mid": v(65.52, -43.83) * mm, "end": v(65.36, -43.7) * mm});
            skArc(sketch, "E275.trimOffspring", {"start": v(65.5, -44.87) * mm, "mid": v(65.63, -44.7) * mm, "end": v(65.7, -44.52) * mm});
            skLineSegment(sketch, "E276", {"start": v(60.93, -42.11) * mm, "end": v(61.29, -42.89) * mm});
            skLineSegment(sketch, "E277", {"start": v(61.29, -42.89) * mm, "end": v(62.68, -43.08) * mm});
            skLineSegment(sketch, "E278", {"start": v(62.68, -43.08) * mm, "end": v(61.77, -42) * mm});
            skLineSegment(sketch, "E279", {"start": v(61.77, -42) * mm, "end": v(60.93, -42.11) * mm});
            skLineSegment(sketch, "E280", {"start": v(65.84, -39.81) * mm, "end": v(66.2, -40.58) * mm});
            skLineSegment(sketch, "E281", {"start": v(66.2, -40.58) * mm, "end": v(65.46, -41.77) * mm});
            skLineSegment(sketch, "E282", {"start": v(65.46, -41.77) * mm, "end": v(65.22, -40.4) * mm});
            skLineSegment(sketch, "E283", {"start": v(65.22, -40.4) * mm, "end": v(65.84, -39.81) * mm});
            skLineSegment(sketch, "E284", {"start": v(66.93, -48.53) * mm, "end": v(67.09, -47.7) * mm});
            skLineSegment(sketch, "E285", {"start": v(67.09, -47.7) * mm, "end": v(66.08, -46.72) * mm});
            skLineSegment(sketch, "E286", {"start": v(66.08, -46.72) * mm, "end": v(66.18, -48.11) * mm});
            skLineSegment(sketch, "E287", {"start": v(66.18, -48.11) * mm, "end": v(66.93, -48.53) * mm});
            skLineSegment(sketch, "E288", {"start": v(69.55, -43.78) * mm, "end": v(68.8, -43.36) * mm});
            skLineSegment(sketch, "E289", {"start": v(68.8, -43.36) * mm, "end": v(67.56, -44.02) * mm});
            skLineSegment(sketch, "E290", {"start": v(67.56, -44.02) * mm, "end": v(68.93, -44.36) * mm});
            skLineSegment(sketch, "E291", {"start": v(68.93, -44.36) * mm, "end": v(69.55, -43.78) * mm});
            skLineSegment(sketch, "E292", {"start": v(61.6, -47.5) * mm, "end": v(62.44, -47.4) * mm});
            skLineSegment(sketch, "E293", {"start": v(62.44, -47.4) * mm, "end": v(63.06, -46.13) * mm});
            skLineSegment(sketch, "E294", {"start": v(63.06, -46.13) * mm, "end": v(61.76, -46.66) * mm});
            skLineSegment(sketch, "E295", {"start": v(61.76, -46.66) * mm, "end": v(61.6, -47.5) * mm});
            skLineSegment(sketch, "E296", {"start": v(33.67, 44) * mm, "end": v(34.76, 41.7) * mm});
            skLineSegment(sketch, "E297", {"start": v(34.76, 41.7) * mm, "end": v(38.18, 41.21) * mm});
            skLineSegment(sketch, "E298", {"start": v(38.44, 41.68) * mm, "end": v(36.21, 44.32) * mm});
            skLineSegment(sketch, "E299", {"start": v(36.21, 44.32) * mm, "end": v(33.67, 44) * mm});
            skLineSegment(sketch, "E300", {"start": v(34.54, 37) * mm, "end": v(37.08, 37.33) * mm});
            skLineSegment(sketch, "E301", {"start": v(37.08, 37.33) * mm, "end": v(38.6, 40.43) * mm});
            skLineSegment(sketch, "E302", {"start": v(38.23, 40.82) * mm, "end": v(35.03, 39.52) * mm});
            skLineSegment(sketch, "E303", {"start": v(35.03, 39.52) * mm, "end": v(34.54, 37) * mm});
            skLineSegment(sketch, "E304", {"start": v(41.47, 35.67) * mm, "end": v(41.95, 38.19) * mm});
            skLineSegment(sketch, "E305", {"start": v(41.95, 38.19) * mm, "end": v(39.47, 40.59) * mm});
            skLineSegment(sketch, "E306", {"start": v(38.98, 40.36) * mm, "end": v(39.23, 36.92) * mm});
            skLineSegment(sketch, "E307", {"start": v(39.23, 36.92) * mm, "end": v(41.47, 35.67) * mm});
            skLineSegment(sketch, "E308", {"start": v(39.65, 40.93) * mm, "end": v(43, 40.1) * mm});
            skLineSegment(sketch, "E309", {"start": v(43, 40.1) * mm, "end": v(44.88, 41.85) * mm});
            skLineSegment(sketch, "E310", {"start": v(39.59, 41.46) * mm, "end": v(42.64, 43.08) * mm});
            skLineSegment(sketch, "E311", {"start": v(42.64, 43.08) * mm, "end": v(44.88, 41.85) * mm});
            skLineSegment(sketch, "E312", {"start": v(40.06, 47) * mm, "end": v(41.14, 44.68) * mm});
            skLineSegment(sketch, "E313", {"start": v(41.14, 44.68) * mm, "end": v(39.32, 41.75) * mm});
            skLineSegment(sketch, "E314", {"start": v(38.8, 41.85) * mm, "end": v(38.2, 45.25) * mm});
            skLineSegment(sketch, "E315", {"start": v(38.2, 45.25) * mm, "end": v(40.06, 47) * mm});
            skArc(sketch, "E316", {"start": v(38.6, 40.43) * mm, "mid": v(38.78, 40.37) * mm, "end": v(38.98, 40.36) * mm});
            skArc(sketch, "E317.trimOffspring", {"start": v(38.18, 41.21) * mm, "mid": v(38.18, 41.02) * mm, "end": v(38.23, 40.82) * mm});
            skArc(sketch, "E318.trimOffspring", {"start": v(38.8, 41.85) * mm, "mid": v(38.6, 41.79) * mm, "end": v(38.44, 41.68) * mm});
            skArc(sketch, "E319.trimOffspring", {"start": v(39.59, 41.46) * mm, "mid": v(39.47, 41.62) * mm, "end": v(39.32, 41.75) * mm});
            skArc(sketch, "E320.trimOffspring", {"start": v(39.47, 40.59) * mm, "mid": v(39.58, 40.75) * mm, "end": v(39.65, 40.93) * mm});
            skLineSegment(sketch, "E321", {"start": v(34.88, 43.34) * mm, "end": v(35.25, 42.57) * mm});
            skLineSegment(sketch, "E322", {"start": v(35.25, 42.57) * mm, "end": v(36.63, 42.37) * mm});
            skLineSegment(sketch, "E323", {"start": v(36.63, 42.37) * mm, "end": v(35.73, 43.44) * mm});
            skLineSegment(sketch, "E324", {"start": v(35.73, 43.44) * mm, "end": v(34.88, 43.34) * mm});
            skLineSegment(sketch, "E325", {"start": v(39.8, 45.64) * mm, "end": v(40.16, 44.87) * mm});
            skLineSegment(sketch, "E326", {"start": v(40.16, 44.87) * mm, "end": v(39.42, 43.68) * mm});
            skLineSegment(sketch, "E327", {"start": v(39.42, 43.68) * mm, "end": v(39.18, 45.06) * mm});
            skLineSegment(sketch, "E328", {"start": v(39.18, 45.06) * mm, "end": v(39.8, 45.64) * mm});
            skLineSegment(sketch, "E329", {"start": v(40.88, 36.93) * mm, "end": v(41.04, 37.76) * mm});
            skLineSegment(sketch, "E330", {"start": v(41.04, 37.76) * mm, "end": v(40.04, 38.74) * mm});
            skLineSegment(sketch, "E331", {"start": v(40.04, 38.74) * mm, "end": v(40.14, 37.34) * mm});
            skLineSegment(sketch, "E332", {"start": v(40.14, 37.34) * mm, "end": v(40.88, 36.93) * mm});
            skLineSegment(sketch, "E333", {"start": v(43.5, 41.68) * mm, "end": v(42.76, 42.09) * mm});
            skLineSegment(sketch, "E334", {"start": v(42.76, 42.09) * mm, "end": v(41.52, 41.43) * mm});
            skLineSegment(sketch, "E335", {"start": v(41.52, 41.43) * mm, "end": v(42.88, 41.1) * mm});
            skLineSegment(sketch, "E336", {"start": v(42.88, 41.1) * mm, "end": v(43.5, 41.68) * mm});
            skLineSegment(sketch, "E337", {"start": v(35.55, 37.95) * mm, "end": v(36.4, 38.06) * mm});
            skLineSegment(sketch, "E338", {"start": v(36.4, 38.06) * mm, "end": v(37.01, 39.32) * mm});
            skLineSegment(sketch, "E339", {"start": v(37.01, 39.32) * mm, "end": v(35.72, 38.8) * mm});
            skLineSegment(sketch, "E340", {"start": v(35.72, 38.8) * mm, "end": v(35.55, 37.95) * mm});
            skLineSegment(sketch, "E341", {"start": v(-4.64, 68.37) * mm, "end": v(-3.97, 65.9) * mm});
            skLineSegment(sketch, "E342", {"start": v(-3.97, 65.9) * mm, "end": v(-0.69, 64.84) * mm});
            skLineSegment(sketch, "E343", {"start": v(-0.35, 65.25) * mm, "end": v(-2.09, 68.24) * mm});
            skLineSegment(sketch, "E344", {"start": v(-2.09, 68.24) * mm, "end": v(-4.64, 68.37) * mm});
            skLineSegment(sketch, "E345", {"start": v(-5, 61.33) * mm, "end": v(-2.44, 61.2) * mm});
            skLineSegment(sketch, "E346", {"start": v(-2.44, 61.2) * mm, "end": v(-0.41, 64) * mm});
            skLineSegment(sketch, "E347", {"start": v(-0.7, 64.45) * mm, "end": v(-4.08, 63.72) * mm});
            skLineSegment(sketch, "E348", {"start": v(-4.08, 63.72) * mm, "end": v(-5, 61.33) * mm});
            skLineSegment(sketch, "E349", {"start": v(1.59, 58.81) * mm, "end": v(2.5, 61.2) * mm});
            skLineSegment(sketch, "E350", {"start": v(2.5, 61.2) * mm, "end": v(0.47, 64) * mm});
            skLineSegment(sketch, "E351", {"start": v(-0.05, 63.86) * mm, "end": v(-0.4, 60.42) * mm});
            skLineSegment(sketch, "E352", {"start": v(-0.4, 60.42) * mm, "end": v(1.59, 58.81) * mm});
            skLineSegment(sketch, "E353", {"start": v(0.71, 64.3) * mm, "end": v(3.87, 62.9) * mm});
            skLineSegment(sketch, "E354", {"start": v(3.87, 62.9) * mm, "end": v(6.02, 64.3) * mm});
            skLineSegment(sketch, "E355", {"start": v(0.74, 64.84) * mm, "end": v(4.02, 65.9) * mm});
            skLineSegment(sketch, "E356", {"start": v(4.02, 65.9) * mm, "end": v(6.02, 64.3) * mm});
            skLineSegment(sketch, "E357", {"start": v(2.17, 70.21) * mm, "end": v(2.83, 67.74) * mm});
            skLineSegment(sketch, "E358", {"start": v(2.83, 67.74) * mm, "end": v(0.53, 65.16) * mm});
            skLineSegment(sketch, "E359", {"start": v(0.03, 65.36) * mm, "end": v(0.03, 68.8) * mm});
            skLineSegment(sketch, "E360", {"start": v(0.03, 68.8) * mm, "end": v(2.17, 70.21) * mm});
            skArc(sketch, "E361", {"start": v(-0.41, 64) * mm, "mid": v(-0.24, 63.9) * mm, "end": v(-0.05, 63.86) * mm});
            skArc(sketch, "E362.trimOffspring", {"start": v(-0.69, 64.84) * mm, "mid": v(-0.72, 64.64) * mm, "end": v(-0.7, 64.45) * mm});
            skArc(sketch, "E363.trimOffspring", {"start": v(0.03, 65.36) * mm, "mid": v(-0.17, 65.33) * mm, "end": v(-0.35, 65.25) * mm});
            skArc(sketch, "E364.trimOffspring", {"start": v(0.74, 64.84) * mm, "mid": v(0.65, 65.02) * mm, "end": v(0.53, 65.16) * mm});
            skArc(sketch, "E365.trimOffspring", {"start": v(0.47, 64) * mm, "mid": v(0.61, 64.13) * mm, "end": v(0.71, 64.3) * mm});
            skLineSegment(sketch, "E366", {"start": v(-3.57, 67.5) * mm, "end": v(-3.34, 66.68) * mm});
            skLineSegment(sketch, "E367", {"start": v(-3.34, 66.68) * mm, "end": v(-2.01, 66.25) * mm});
            skLineSegment(sketch, "E368", {"start": v(-2.01, 66.25) * mm, "end": v(-2.72, 67.46) * mm});
            skLineSegment(sketch, "E369", {"start": v(-2.72, 67.46) * mm, "end": v(-3.57, 67.5) * mm});
            skLineSegment(sketch, "E370", {"start": v(1.67, 68.92) * mm, "end": v(1.9, 68.1) * mm});
            skLineSegment(sketch, "E371", {"start": v(1.9, 68.1) * mm, "end": v(0.96, 67.05) * mm});
            skLineSegment(sketch, "E372", {"start": v(0.96, 67.05) * mm, "end": v(0.96, 68.45) * mm});
            skLineSegment(sketch, "E373", {"start": v(0.96, 68.45) * mm, "end": v(1.67, 68.92) * mm});
            skLineSegment(sketch, "E374", {"start": v(1.23, 60.15) * mm, "end": v(1.53, 60.94) * mm});
            skLineSegment(sketch, "E375", {"start": v(1.53, 60.94) * mm, "end": v(0.7, 62.08) * mm});
            skLineSegment(sketch, "E376", {"start": v(0.7, 62.08) * mm, "end": v(0.57, 60.68) * mm});
            skLineSegment(sketch, "E377", {"start": v(0.57, 60.68) * mm, "end": v(1.23, 60.15) * mm});
            skLineSegment(sketch, "E378", {"start": v(4.64, 64.37) * mm, "end": v(3.97, 64.9) * mm});
            skLineSegment(sketch, "E379", {"start": v(3.97, 64.9) * mm, "end": v(2.64, 64.47) * mm});
            skLineSegment(sketch, "E380", {"start": v(2.64, 64.47) * mm, "end": v(3.92, 63.9) * mm});
            skLineSegment(sketch, "E381", {"start": v(3.92, 63.9) * mm, "end": v(4.64, 64.37) * mm});
            skLineSegment(sketch, "E382", {"start": v(-3.84, 62.08) * mm, "end": v(-3, 62.04) * mm});
            skLineSegment(sketch, "E383", {"start": v(-3, 62.04) * mm, "end": v(-2.17, 63.18) * mm});
            skLineSegment(sketch, "E384", {"start": v(-2.17, 63.18) * mm, "end": v(-3.54, 62.88) * mm});
            skLineSegment(sketch, "E385", {"start": v(-3.54, 62.88) * mm, "end": v(-3.84, 62.08) * mm});
            skLineSegment(sketch, "E386", {"start": v(7.71, 53.9) * mm, "end": v(7.94, 51.36) * mm});
            skLineSegment(sketch, "E387", {"start": v(7.94, 51.36) * mm, "end": v(11, 49.74) * mm});
            skLineSegment(sketch, "E388", {"start": v(11.4, 50.1) * mm, "end": v(10.2, 53.33) * mm});
            skLineSegment(sketch, "E389", {"start": v(10.2, 53.33) * mm, "end": v(7.71, 53.9) * mm});
            skLineSegment(sketch, "E390", {"start": v(6.14, 47.03) * mm, "end": v(8.63, 46.47) * mm});
            skLineSegment(sketch, "E391", {"start": v(8.63, 46.47) * mm, "end": v(11.12, 48.87) * mm});
            skLineSegment(sketch, "E392", {"start": v(10.9, 49.36) * mm, "end": v(7.45, 49.23) * mm});
            skLineSegment(sketch, "E393", {"start": v(7.45, 49.23) * mm, "end": v(6.14, 47.03) * mm});
            skLineSegment(sketch, "E394", {"start": v(12.19, 43.41) * mm, "end": v(13.5, 45.6) * mm});
            skLineSegment(sketch, "E395", {"start": v(13.5, 45.6) * mm, "end": v(11.98, 48.71) * mm});
            skLineSegment(sketch, "E396", {"start": v(11.45, 48.67) * mm, "end": v(10.5, 45.34) * mm});
            skLineSegment(sketch, "E397", {"start": v(10.5, 45.34) * mm, "end": v(12.19, 43.41) * mm});
            skLineSegment(sketch, "E398", {"start": v(12.28, 48.97) * mm, "end": v(15.15, 47.05) * mm});
            skLineSegment(sketch, "E399", {"start": v(15.15, 47.05) * mm, "end": v(17.5, 48.05) * mm});
            skLineSegment(sketch, "E400", {"start": v(12.4, 49.5) * mm, "end": v(15.82, 49.97) * mm});
            skLineSegment(sketch, "E401", {"start": v(15.82, 49.97) * mm, "end": v(17.5, 48.05) * mm});
            skLineSegment(sketch, "E402", {"start": v(14.74, 54.54) * mm, "end": v(14.96, 51.99) * mm});
            skLineSegment(sketch, "E403", {"start": v(14.96, 51.99) * mm, "end": v(12.24, 49.85) * mm});
            skLineSegment(sketch, "E404", {"start": v(11.78, 50.13) * mm, "end": v(12.38, 53.53) * mm});
            skLineSegment(sketch, "E405", {"start": v(12.38, 53.53) * mm, "end": v(14.74, 54.54) * mm});
            skArc(sketch, "E406", {"start": v(11.12, 48.87) * mm, "mid": v(11.27, 48.74) * mm, "end": v(11.45, 48.67) * mm});
            skArc(sketch, "E407.trimOffspring", {"start": v(11, 49.74) * mm, "mid": v(10.92, 49.55) * mm, "end": v(10.9, 49.36) * mm});
            skArc(sketch, "E408.trimOffspring", {"start": v(11.78, 50.13) * mm, "mid": v(11.59, 50.13) * mm, "end": v(11.4, 50.1) * mm});
            skArc(sketch, "E409.trimOffspring", {"start": v(12.4, 49.5) * mm, "mid": v(12.34, 49.68) * mm, "end": v(12.24, 49.85) * mm});
            skArc(sketch, "E410.trimOffspring", {"start": v(11.98, 48.71) * mm, "mid": v(12.15, 48.82) * mm, "end": v(12.28, 48.97) * mm});
            skLineSegment(sketch, "E411", {"start": v(8.62, 52.87) * mm, "end": v(8.7, 52.02) * mm});
            skLineSegment(sketch, "E412", {"start": v(8.7, 52.02) * mm, "end": v(9.93, 51.36) * mm});
            skLineSegment(sketch, "E413", {"start": v(9.93, 51.36) * mm, "end": v(9.45, 52.68) * mm});
            skLineSegment(sketch, "E414", {"start": v(9.45, 52.68) * mm, "end": v(8.62, 52.87) * mm});
            skLineSegment(sketch, "E415", {"start": v(14.03, 53.35) * mm, "end": v(14.1, 52.5) * mm});
            skLineSegment(sketch, "E416", {"start": v(14.1, 52.5) * mm, "end": v(13, 51.63) * mm});
            skLineSegment(sketch, "E417", {"start": v(13, 51.63) * mm, "end": v(13.24, 53.01) * mm});
            skLineSegment(sketch, "E418", {"start": v(13.24, 53.01) * mm, "end": v(14.03, 53.35) * mm});
            skLineSegment(sketch, "E419", {"start": v(12.06, 44.79) * mm, "end": v(12.5, 45.52) * mm});
            skLineSegment(sketch, "E420", {"start": v(12.5, 45.52) * mm, "end": v(11.89, 46.78) * mm});
            skLineSegment(sketch, "E421", {"start": v(11.89, 46.78) * mm, "end": v(11.5, 45.43) * mm});
            skLineSegment(sketch, "E422", {"start": v(11.5, 45.43) * mm, "end": v(12.06, 44.79) * mm});
            skLineSegment(sketch, "E423", {"start": v(16.16, 48.36) * mm, "end": v(15.6, 49) * mm});
            skLineSegment(sketch, "E424", {"start": v(15.6, 49) * mm, "end": v(14.2, 48.8) * mm});
            skLineSegment(sketch, "E425", {"start": v(14.2, 48.8) * mm, "end": v(15.37, 48.02) * mm});
            skLineSegment(sketch, "E426", {"start": v(15.37, 48.02) * mm, "end": v(16.16, 48.36) * mm});
            skLineSegment(sketch, "E427", {"start": v(7.4, 47.58) * mm, "end": v(8.24, 47.39) * mm});
            skLineSegment(sketch, "E428", {"start": v(8.24, 47.39) * mm, "end": v(9.25, 48.36) * mm});
            skLineSegment(sketch, "E429", {"start": v(9.25, 48.36) * mm, "end": v(7.85, 48.3) * mm});
            skLineSegment(sketch, "E430", {"start": v(7.85, 48.3) * mm, "end": v(7.4, 47.58) * mm});
            skLineSegment(sketch, "E431", {"start": v(-6.66, 39.15) * mm, "end": v(-5.18, 37.06) * mm});
            skLineSegment(sketch, "E432", {"start": v(-5.18, 37.06) * mm, "end": v(-1.73, 37.18) * mm});
            skLineSegment(sketch, "E433", {"start": v(-1.56, 37.68) * mm, "end": v(-4.21, 39.9) * mm});
            skLineSegment(sketch, "E434", {"start": v(-4.21, 39.9) * mm, "end": v(-6.66, 39.15) * mm});
            skLineSegment(sketch, "E435", {"start": v(-4.59, 32.4) * mm, "end": v(-2.14, 33.16) * mm});
            skLineSegment(sketch, "E436", {"start": v(-2.14, 33.16) * mm, "end": v(-1.19, 36.48) * mm});
            skLineSegment(sketch, "E437", {"start": v(-1.62, 36.8) * mm, "end": v(-4.54, 34.96) * mm});
            skLineSegment(sketch, "E438", {"start": v(-4.54, 34.96) * mm, "end": v(-4.59, 32.4) * mm});
            skLineSegment(sketch, "E439", {"start": v(2.47, 32.3) * mm, "end": v(2.5, 34.85) * mm});
            skLineSegment(sketch, "E440", {"start": v(2.5, 34.85) * mm, "end": v(-0.36, 36.78) * mm});
            skLineSegment(sketch, "E441", {"start": v(-0.8, 36.48) * mm, "end": v(0.05, 33.13) * mm});
            skLineSegment(sketch, "E442", {"start": v(0.05, 33.13) * mm, "end": v(2.47, 32.3) * mm});
            skLineSegment(sketch, "E443", {"start": v(-0.23, 37.15) * mm, "end": v(3.21, 36.92) * mm});
            skLineSegment(sketch, "E444", {"start": v(3.21, 36.92) * mm, "end": v(4.75, 38.97) * mm});
            skLineSegment(sketch, "E445", {"start": v(-0.4, 37.66) * mm, "end": v(2.33, 39.8) * mm});
            skLineSegment(sketch, "E446", {"start": v(2.33, 39.8) * mm, "end": v(4.75, 38.97) * mm});
            skLineSegment(sketch, "E447", {"start": v(-0.89, 43.2) * mm, "end": v(0.58, 41.1) * mm});
            skLineSegment(sketch, "E448", {"start": v(0.58, 41.1) * mm, "end": v(-0.7, 37.9) * mm});
            skLineSegment(sketch, "E449", {"start": v(-1.24, 37.9) * mm, "end": v(-2.42, 41.15) * mm});
            skLineSegment(sketch, "E450", {"start": v(-2.42, 41.15) * mm, "end": v(-0.89, 43.2) * mm});
            skArc(sketch, "E451", {"start": v(-1.19, 36.48) * mm, "mid": v(-1, 36.45) * mm, "end": v(-0.8, 36.48) * mm});
            skArc(sketch, "E452.trimOffspring", {"start": v(-1.73, 37.18) * mm, "mid": v(-1.7, 36.98) * mm, "end": v(-1.62, 36.8) * mm});
            skArc(sketch, "E453.trimOffspring", {"start": v(-1.24, 37.9) * mm, "mid": v(-1.41, 37.82) * mm, "end": v(-1.56, 37.68) * mm});
            skArc(sketch, "E454.trimOffspring", {"start": v(-0.4, 37.66) * mm, "mid": v(-0.53, 37.8) * mm, "end": v(-0.7, 37.9) * mm});
            skArc(sketch, "E455.trimOffspring", {"start": v(-0.36, 36.78) * mm, "mid": v(-0.27, 36.96) * mm, "end": v(-0.23, 37.15) * mm});
            skLineSegment(sketch, "E456", {"start": v(-5.35, 38.7) * mm, "end": v(-4.86, 38) * mm});
            skLineSegment(sketch, "E457", {"start": v(-4.86, 38) * mm, "end": v(-3.46, 38.05) * mm});
            skLineSegment(sketch, "E458", {"start": v(-3.46, 38.05) * mm, "end": v(-4.54, 38.95) * mm});
            skLineSegment(sketch, "E459", {"start": v(-4.54, 38.95) * mm, "end": v(-5.35, 38.7) * mm});
            skLineSegment(sketch, "E460", {"start": v(-0.9, 41.82) * mm, "end": v(-0.42, 41.12) * mm});
            skLineSegment(sketch, "E461", {"start": v(-0.42, 41.12) * mm, "end": v(-0.94, 39.82) * mm});
            skLineSegment(sketch, "E462", {"start": v(-0.94, 39.82) * mm, "end": v(-1.42, 41.14) * mm});
            skLineSegment(sketch, "E463", {"start": v(-1.42, 41.14) * mm, "end": v(-0.9, 41.82) * mm});
            skLineSegment(sketch, "E464", {"start": v(1.67, 33.42) * mm, "end": v(1.68, 34.28) * mm});
            skLineSegment(sketch, "E465", {"start": v(1.68, 34.28) * mm, "end": v(0.52, 35.06) * mm});
            skLineSegment(sketch, "E466", {"start": v(0.52, 35.06) * mm, "end": v(0.87, 33.7) * mm});
            skLineSegment(sketch, "E467", {"start": v(0.87, 33.7) * mm, "end": v(1.67, 33.42) * mm});
            skLineSegment(sketch, "E468", {"start": v(3.43, 38.56) * mm, "end": v(2.62, 38.84) * mm});
            skLineSegment(sketch, "E469", {"start": v(2.62, 38.84) * mm, "end": v(1.52, 37.97) * mm});
            skLineSegment(sketch, "E470", {"start": v(1.52, 37.97) * mm, "end": v(2.92, 37.88) * mm});
            skLineSegment(sketch, "E471", {"start": v(2.92, 37.88) * mm, "end": v(3.43, 38.56) * mm});
            skLineSegment(sketch, "E472", {"start": v(-3.76, 33.5) * mm, "end": v(-2.94, 33.76) * mm});
            skLineSegment(sketch, "E473", {"start": v(-2.94, 33.76) * mm, "end": v(-2.55, 35.1) * mm});
            skLineSegment(sketch, "E474", {"start": v(-2.55, 35.1) * mm, "end": v(-3.74, 34.36) * mm});
            skLineSegment(sketch, "E475", {"start": v(-3.74, 34.36) * mm, "end": v(-3.76, 33.5) * mm});
            skLineSegment(sketch, "E476", {"start": v(-21.83, 47.83) * mm, "end": v(-21.16, 45.36) * mm});
            skLineSegment(sketch, "E477", {"start": v(-21.16, 45.36) * mm, "end": v(-17.88, 44.3) * mm});
            skLineSegment(sketch, "E478", {"start": v(-17.54, 44.7) * mm, "end": v(-19.28, 47.7) * mm});
            skLineSegment(sketch, "E479", {"start": v(-19.28, 47.7) * mm, "end": v(-21.83, 47.83) * mm});
            skLineSegment(sketch, "E480", {"start": v(-22.2, 40.78) * mm, "end": v(-19.64, 40.66) * mm});
            skLineSegment(sketch, "E481", {"start": v(-19.64, 40.66) * mm, "end": v(-17.6, 43.45) * mm});
            skLineSegment(sketch, "E482", {"start": v(-17.9, 43.9) * mm, "end": v(-21.27, 43.17) * mm});
            skLineSegment(sketch, "E483", {"start": v(-21.27, 43.17) * mm, "end": v(-22.2, 40.78) * mm});
            skLineSegment(sketch, "E484", {"start": v(-15.6, 38.27) * mm, "end": v(-14.7, 40.66) * mm});
            skLineSegment(sketch, "E485", {"start": v(-14.7, 40.66) * mm, "end": v(-16.72, 43.45) * mm});
            skLineSegment(sketch, "E486", {"start": v(-17.24, 43.31) * mm, "end": v(-17.6, 39.88) * mm});
            skLineSegment(sketch, "E487", {"start": v(-17.6, 39.88) * mm, "end": v(-15.6, 38.27) * mm});
            skLineSegment(sketch, "E488", {"start": v(-16.48, 43.76) * mm, "end": v(-13.32, 42.36) * mm});
            skLineSegment(sketch, "E489", {"start": v(-13.32, 42.36) * mm, "end": v(-11.17, 43.76) * mm});
            skLineSegment(sketch, "E490", {"start": v(-16.45, 44.3) * mm, "end": v(-13.17, 45.36) * mm});
            skLineSegment(sketch, "E491", {"start": v(-13.17, 45.36) * mm, "end": v(-11.17, 43.76) * mm});
            skLineSegment(sketch, "E492", {"start": v(-15.02, 49.66) * mm, "end": v(-14.36, 47.2) * mm});
            skLineSegment(sketch, "E493", {"start": v(-14.36, 47.2) * mm, "end": v(-16.67, 44.62) * mm});
            skLineSegment(sketch, "E494", {"start": v(-17.17, 44.8) * mm, "end": v(-17.17, 48.26) * mm});
            skLineSegment(sketch, "E495", {"start": v(-17.17, 48.26) * mm, "end": v(-15.02, 49.66) * mm});
            skArc(sketch, "E496", {"start": v(-17.6, 43.45) * mm, "mid": v(-17.43, 43.36) * mm, "end": v(-17.24, 43.31) * mm});
            skArc(sketch, "E497.trimOffspring", {"start": v(-17.88, 44.3) * mm, "mid": v(-17.91, 44.1) * mm, "end": v(-17.9, 43.9) * mm});
            skArc(sketch, "E498.trimOffspring", {"start": v(-17.17, 44.8) * mm, "mid": v(-17.36, 44.78) * mm, "end": v(-17.54, 44.7) * mm});
            skArc(sketch, "E499.trimOffspring", {"start": v(-16.45, 44.3) * mm, "mid": v(-16.54, 44.47) * mm, "end": v(-16.67, 44.62) * mm});
            skArc(sketch, "E500.trimOffspring", {"start": v(-16.72, 43.45) * mm, "mid": v(-16.58, 43.59) * mm, "end": v(-16.48, 43.76) * mm});
            skLineSegment(sketch, "E501", {"start": v(-20.76, 46.96) * mm, "end": v(-20.54, 46.14) * mm});
            skLineSegment(sketch, "E502", {"start": v(-20.54, 46.14) * mm, "end": v(-19.2, 45.7) * mm});
            skLineSegment(sketch, "E503", {"start": v(-19.2, 45.7) * mm, "end": v(-19.9, 46.91) * mm});
            skLineSegment(sketch, "E504", {"start": v(-19.9, 46.91) * mm, "end": v(-20.76, 46.96) * mm});
            skLineSegment(sketch, "E505", {"start": v(-15.52, 48.37) * mm, "end": v(-15.3, 47.55) * mm});
            skLineSegment(sketch, "E506", {"start": v(-15.3, 47.55) * mm, "end": v(-16.23, 46.5) * mm});
            skLineSegment(sketch, "E507", {"start": v(-16.23, 46.5) * mm, "end": v(-16.23, 47.9) * mm});
            skLineSegment(sketch, "E508", {"start": v(-16.23, 47.9) * mm, "end": v(-15.52, 48.37) * mm});
            skLineSegment(sketch, "E509", {"start": v(-15.96, 39.6) * mm, "end": v(-15.66, 40.4) * mm});
            skLineSegment(sketch, "E510", {"start": v(-15.66, 40.4) * mm, "end": v(-16.48, 41.53) * mm});
            skLineSegment(sketch, "E511", {"start": v(-16.48, 41.53) * mm, "end": v(-16.63, 40.14) * mm});
            skLineSegment(sketch, "E512", {"start": v(-16.63, 40.14) * mm, "end": v(-15.96, 39.6) * mm});
            skLineSegment(sketch, "E513", {"start": v(-12.55, 43.83) * mm, "end": v(-13.22, 44.36) * mm});
            skLineSegment(sketch, "E514", {"start": v(-13.22, 44.36) * mm, "end": v(-14.55, 43.93) * mm});
            skLineSegment(sketch, "E515", {"start": v(-14.55, 43.93) * mm, "end": v(-13.27, 43.36) * mm});
            skLineSegment(sketch, "E516", {"start": v(-13.27, 43.36) * mm, "end": v(-12.55, 43.83) * mm});
            skLineSegment(sketch, "E517", {"start": v(-21.03, 41.54) * mm, "end": v(-20.18, 41.5) * mm});
            skLineSegment(sketch, "E518", {"start": v(-20.18, 41.5) * mm, "end": v(-19.36, 42.63) * mm});
            skLineSegment(sketch, "E519", {"start": v(-19.36, 42.63) * mm, "end": v(-20.73, 42.33) * mm});
            skLineSegment(sketch, "E520", {"start": v(-20.73, 42.33) * mm, "end": v(-21.03, 41.54) * mm});
            skLineSegment(sketch, "E521", {"start": v(-38.71, 38.5) * mm, "end": v(-37.43, 36.3) * mm});
            skLineSegment(sketch, "E522", {"start": v(-37.43, 36.3) * mm, "end": v(-33.98, 36.11) * mm});
            skLineSegment(sketch, "E523", {"start": v(-33.76, 36.6) * mm, "end": v(-36.2, 39.03) * mm});
            skLineSegment(sketch, "E524", {"start": v(-36.2, 39.03) * mm, "end": v(-38.71, 38.5) * mm});
            skLineSegment(sketch, "E525", {"start": v(-37.23, 31.6) * mm, "end": v(-34.73, 32.15) * mm});
            skLineSegment(sketch, "E526", {"start": v(-34.73, 32.15) * mm, "end": v(-33.5, 35.37) * mm});
            skLineSegment(sketch, "E527", {"start": v(-33.9, 35.73) * mm, "end": v(-36.97, 34.15) * mm});
            skLineSegment(sketch, "E528", {"start": v(-36.97, 34.15) * mm, "end": v(-37.23, 31.6) * mm});
            skLineSegment(sketch, "E529", {"start": v(-30.22, 30.88) * mm, "end": v(-29.96, 33.43) * mm});
            skLineSegment(sketch, "E530", {"start": v(-29.96, 33.43) * mm, "end": v(-32.64, 35.6) * mm});
            skLineSegment(sketch, "E531", {"start": v(-33.1, 35.33) * mm, "end": v(-32.56, 31.92) * mm});
            skLineSegment(sketch, "E532", {"start": v(-32.56, 31.92) * mm, "end": v(-30.22, 30.88) * mm});
            skLineSegment(sketch, "E533", {"start": v(-32.49, 35.96) * mm, "end": v(-29.07, 35.43) * mm});
            skLineSegment(sketch, "E534", {"start": v(-29.07, 35.43) * mm, "end": v(-27.36, 37.33) * mm});
            skLineSegment(sketch, "E535", {"start": v(-32.6, 36.48) * mm, "end": v(-29.7, 38.36) * mm});
            skLineSegment(sketch, "E536", {"start": v(-29.7, 38.36) * mm, "end": v(-27.36, 37.33) * mm});
            skLineSegment(sketch, "E537", {"start": v(-32.61, 42.04) * mm, "end": v(-31.33, 39.82) * mm});
            skLineSegment(sketch, "E538", {"start": v(-31.33, 39.82) * mm, "end": v(-32.89, 36.74) * mm});
            skLineSegment(sketch, "E539", {"start": v(-33.42, 36.8) * mm, "end": v(-34.32, 40.13) * mm});
            skLineSegment(sketch, "E540", {"start": v(-34.32, 40.13) * mm, "end": v(-32.61, 42.04) * mm});
            skArc(sketch, "E541", {"start": v(-33.5, 35.37) * mm, "mid": v(-33.3, 35.33) * mm, "end": v(-33.1, 35.33) * mm});
            skArc(sketch, "E542.trimOffspring", {"start": v(-33.98, 36.11) * mm, "mid": v(-33.96, 35.91) * mm, "end": v(-33.9, 35.73) * mm});
            skArc(sketch, "E543.trimOffspring", {"start": v(-33.42, 36.8) * mm, "mid": v(-33.6, 36.72) * mm, "end": v(-33.76, 36.6) * mm});
            skArc(sketch, "E544.trimOffspring", {"start": v(-32.6, 36.48) * mm, "mid": v(-32.73, 36.63) * mm, "end": v(-32.89, 36.74) * mm});
            skArc(sketch, "E545.trimOffspring", {"start": v(-32.64, 35.6) * mm, "mid": v(-32.54, 35.77) * mm, "end": v(-32.49, 35.96) * mm});
            skLineSegment(sketch, "E546", {"start": v(-37.45, 37.94) * mm, "end": v(-37.02, 37.2) * mm});
            skLineSegment(sketch, "E547", {"start": v(-37.02, 37.2) * mm, "end": v(-35.62, 37.13) * mm});
            skLineSegment(sketch, "E548", {"start": v(-35.62, 37.13) * mm, "end": v(-36.62, 38.12) * mm});
            skLineSegment(sketch, "E549", {"start": v(-36.62, 38.12) * mm, "end": v(-37.45, 37.94) * mm});
            skLineSegment(sketch, "E550", {"start": v(-32.75, 40.67) * mm, "end": v(-32.33, 39.93) * mm});
            skLineSegment(sketch, "E551", {"start": v(-32.33, 39.93) * mm, "end": v(-32.96, 38.68) * mm});
            skLineSegment(sketch, "E552", {"start": v(-32.96, 38.68) * mm, "end": v(-33.32, 40.03) * mm});
            skLineSegment(sketch, "E553", {"start": v(-33.32, 40.03) * mm, "end": v(-32.75, 40.67) * mm});
            skLineSegment(sketch, "E554", {"start": v(-30.91, 32.08) * mm, "end": v(-30.83, 32.92) * mm});
            skLineSegment(sketch, "E555", {"start": v(-30.83, 32.92) * mm, "end": v(-31.91, 33.8) * mm});
            skLineSegment(sketch, "E556", {"start": v(-31.91, 33.8) * mm, "end": v(-31.7, 32.42) * mm});
            skLineSegment(sketch, "E557", {"start": v(-31.7, 32.42) * mm, "end": v(-30.91, 32.08) * mm});
            skLineSegment(sketch, "E558", {"start": v(-28.71, 37.04) * mm, "end": v(-29.5, 37.38) * mm});
            skLineSegment(sketch, "E559", {"start": v(-29.5, 37.38) * mm, "end": v(-30.67, 36.62) * mm});
            skLineSegment(sketch, "E560", {"start": v(-30.67, 36.62) * mm, "end": v(-29.28, 36.4) * mm});
            skLineSegment(sketch, "E561", {"start": v(-29.28, 36.4) * mm, "end": v(-28.71, 37.04) * mm});
            skLineSegment(sketch, "E562", {"start": v(-36.31, 32.63) * mm, "end": v(-35.48, 32.82) * mm});
            skLineSegment(sketch, "E563", {"start": v(-35.48, 32.82) * mm, "end": v(-34.98, 34.12) * mm});
            skLineSegment(sketch, "E564", {"start": v(-34.98, 34.12) * mm, "end": v(-36.22, 33.48) * mm});
            skLineSegment(sketch, "E565", {"start": v(-36.22, 33.48) * mm, "end": v(-36.31, 32.63) * mm});
            skLineSegment(sketch, "E566", {"start": v(-50.96, 52.76) * mm, "end": v(-50.95, 50.2) * mm});
            skLineSegment(sketch, "E567", {"start": v(-50.95, 50.2) * mm, "end": v(-48.05, 48.32) * mm});
            skLineSegment(sketch, "E568", {"start": v(-47.62, 48.63) * mm, "end": v(-48.52, 51.96) * mm});
            skLineSegment(sketch, "E569", {"start": v(-48.52, 51.96) * mm, "end": v(-50.96, 52.76) * mm});
            skLineSegment(sketch, "E570", {"start": v(-53.13, 46.04) * mm, "end": v(-50.69, 45.26) * mm});
            skLineSegment(sketch, "E571", {"start": v(-50.69, 45.26) * mm, "end": v(-48, 47.44) * mm});
            skLineSegment(sketch, "E572", {"start": v(-48.17, 47.94) * mm, "end": v(-51.62, 48.11) * mm});
            skLineSegment(sketch, "E573", {"start": v(-51.62, 48.11) * mm, "end": v(-53.13, 46.04) * mm});
            skLineSegment(sketch, "E574", {"start": v(-47.41, 41.9) * mm, "end": v(-45.92, 43.98) * mm});
            skLineSegment(sketch, "E575", {"start": v(-45.92, 43.98) * mm, "end": v(-47.15, 47.2) * mm});
            skLineSegment(sketch, "E576", {"start": v(-47.69, 47.2) * mm, "end": v(-48.92, 43.98) * mm});
            skLineSegment(sketch, "E577", {"start": v(-48.92, 43.98) * mm, "end": v(-47.41, 41.9) * mm});
            skLineSegment(sketch, "E578", {"start": v(-46.84, 47.44) * mm, "end": v(-44.15, 45.27) * mm});
            skLineSegment(sketch, "E579", {"start": v(-44.15, 45.27) * mm, "end": v(-41.71, 46.06) * mm});
            skLineSegment(sketch, "E580", {"start": v(-46.67, 47.95) * mm, "end": v(-43.22, 48.13) * mm});
            skLineSegment(sketch, "E581", {"start": v(-43.22, 48.13) * mm, "end": v(-41.71, 46.06) * mm});
            skLineSegment(sketch, "E582", {"start": v(-43.9, 52.77) * mm, "end": v(-43.9, 50.2) * mm});
            skLineSegment(sketch, "E583", {"start": v(-43.9, 50.2) * mm, "end": v(-46.8, 48.32) * mm});
            skLineSegment(sketch, "E584", {"start": v(-47.23, 48.63) * mm, "end": v(-46.33, 51.97) * mm});
            skLineSegment(sketch, "E585", {"start": v(-46.33, 51.97) * mm, "end": v(-43.9, 52.77) * mm});
            skArc(sketch, "E586", {"start": v(-48, 47.44) * mm, "mid": v(-47.86, 47.3) * mm, "end": v(-47.69, 47.2) * mm});
            skArc(sketch, "E587.trimOffspring", {"start": v(-48.05, 48.32) * mm, "mid": v(-48.14, 48.14) * mm, "end": v(-48.17, 47.94) * mm});
            skArc(sketch, "E588.trimOffspring", {"start": v(-47.23, 48.63) * mm, "mid": v(-47.42, 48.66) * mm, "end": v(-47.62, 48.63) * mm});
            skArc(sketch, "E589.trimOffspring", {"start": v(-46.67, 47.95) * mm, "mid": v(-46.7, 48.14) * mm, "end": v(-46.8, 48.32) * mm});
            skArc(sketch, "E590.trimOffspring", {"start": v(-47.15, 47.2) * mm, "mid": v(-46.98, 47.3) * mm, "end": v(-46.84, 47.44) * mm});
            skLineSegment(sketch, "E591", {"start": v(-50.14, 51.64) * mm, "end": v(-50.14, 50.79) * mm});
            skLineSegment(sketch, "E592", {"start": v(-50.14, 50.79) * mm, "end": v(-48.96, 50.02) * mm});
            skLineSegment(sketch, "E593", {"start": v(-48.96, 50.02) * mm, "end": v(-49.33, 51.38) * mm});
            skLineSegment(sketch, "E594", {"start": v(-49.33, 51.38) * mm, "end": v(-50.14, 51.64) * mm});
            skLineSegment(sketch, "E595", {"start": v(-44.71, 51.65) * mm, "end": v(-44.71, 50.8) * mm});
            skLineSegment(sketch, "E596", {"start": v(-44.71, 50.8) * mm, "end": v(-45.89, 50.03) * mm});
            skLineSegment(sketch, "E597", {"start": v(-45.89, 50.03) * mm, "end": v(-45.52, 51.38) * mm});
            skLineSegment(sketch, "E598", {"start": v(-45.52, 51.38) * mm, "end": v(-44.71, 51.65) * mm});
            skLineSegment(sketch, "E599", {"start": v(-47.41, 43.29) * mm, "end": v(-46.92, 43.98) * mm});
            skLineSegment(sketch, "E600", {"start": v(-46.92, 43.98) * mm, "end": v(-47.42, 45.29) * mm});
            skLineSegment(sketch, "E601", {"start": v(-47.42, 45.29) * mm, "end": v(-47.92, 43.98) * mm});
            skLineSegment(sketch, "E602", {"start": v(-47.92, 43.98) * mm, "end": v(-47.41, 43.29) * mm});
            skLineSegment(sketch, "E603", {"start": v(-43.03, 46.49) * mm, "end": v(-43.53, 47.18) * mm});
            skLineSegment(sketch, "E604", {"start": v(-43.53, 47.18) * mm, "end": v(-44.93, 47.1) * mm});
            skLineSegment(sketch, "E605", {"start": v(-44.93, 47.1) * mm, "end": v(-43.84, 46.22) * mm});
            skLineSegment(sketch, "E606", {"start": v(-43.84, 46.22) * mm, "end": v(-43.03, 46.49) * mm});
            skLineSegment(sketch, "E607", {"start": v(-51.81, 46.47) * mm, "end": v(-51, 46.21) * mm});
            skLineSegment(sketch, "E608", {"start": v(-51, 46.21) * mm, "end": v(-49.91, 47.1) * mm});
            skLineSegment(sketch, "E609", {"start": v(-49.91, 47.1) * mm, "end": v(-51.31, 47.16) * mm});
            skLineSegment(sketch, "E610", {"start": v(-51.31, 47.16) * mm, "end": v(-51.81, 46.47) * mm});
            skLineSegment(sketch, "E611", {"start": v(-68.5, 48.85) * mm, "end": v(-67.82, 46.38) * mm});
            skLineSegment(sketch, "E612", {"start": v(-67.82, 46.38) * mm, "end": v(-64.54, 45.31) * mm});
            skLineSegment(sketch, "E613", {"start": v(-64.2, 45.73) * mm, "end": v(-65.94, 48.71) * mm});
            skLineSegment(sketch, "E614", {"start": v(-65.94, 48.71) * mm, "end": v(-68.5, 48.85) * mm});
            skLineSegment(sketch, "E615", {"start": v(-68.85, 41.8) * mm, "end": v(-66.3, 41.68) * mm});
            skLineSegment(sketch, "E616", {"start": v(-66.3, 41.68) * mm, "end": v(-64.27, 44.47) * mm});
            skLineSegment(sketch, "E617", {"start": v(-64.56, 44.92) * mm, "end": v(-67.93, 44.2) * mm});
            skLineSegment(sketch, "E618", {"start": v(-67.93, 44.2) * mm, "end": v(-68.85, 41.8) * mm});
            skLineSegment(sketch, "E619", {"start": v(-62.26, 39.29) * mm, "end": v(-61.35, 41.68) * mm});
            skLineSegment(sketch, "E620", {"start": v(-61.35, 41.68) * mm, "end": v(-63.38, 44.47) * mm});
            skLineSegment(sketch, "E621", {"start": v(-63.9, 44.33) * mm, "end": v(-64.25, 40.9) * mm});
            skLineSegment(sketch, "E622", {"start": v(-64.25, 40.9) * mm, "end": v(-62.26, 39.29) * mm});
            skLineSegment(sketch, "E623", {"start": v(-63.14, 44.78) * mm, "end": v(-59.98, 43.38) * mm});
            skLineSegment(sketch, "E624", {"start": v(-59.98, 43.38) * mm, "end": v(-57.83, 44.77) * mm});
            skLineSegment(sketch, "E625", {"start": v(-63.11, 45.31) * mm, "end": v(-59.83, 46.38) * mm});
            skLineSegment(sketch, "E626", {"start": v(-59.83, 46.38) * mm, "end": v(-57.83, 44.77) * mm});
            skLineSegment(sketch, "E627", {"start": v(-61.68, 50.68) * mm, "end": v(-61.02, 48.21) * mm});
            skLineSegment(sketch, "E628", {"start": v(-61.02, 48.21) * mm, "end": v(-63.33, 45.64) * mm});
            skLineSegment(sketch, "E629", {"start": v(-63.83, 45.83) * mm, "end": v(-63.83, 49.28) * mm});
            skLineSegment(sketch, "E630", {"start": v(-63.83, 49.28) * mm, "end": v(-61.68, 50.68) * mm});
            skArc(sketch, "E631", {"start": v(-64.27, 44.47) * mm, "mid": v(-64.1, 44.38) * mm, "end": v(-63.9, 44.33) * mm});
            skArc(sketch, "E632.trimOffspring", {"start": v(-64.54, 45.31) * mm, "mid": v(-64.57, 45.12) * mm, "end": v(-64.56, 44.92) * mm});
            skArc(sketch, "E633.trimOffspring", {"start": v(-63.83, 45.83) * mm, "mid": v(-64.02, 45.8) * mm, "end": v(-64.2, 45.73) * mm});
            skArc(sketch, "E634.trimOffspring", {"start": v(-63.11, 45.31) * mm, "mid": v(-63.2, 45.49) * mm, "end": v(-63.33, 45.64) * mm});
            skArc(sketch, "E635.trimOffspring", {"start": v(-63.38, 44.47) * mm, "mid": v(-63.24, 44.6) * mm, "end": v(-63.14, 44.78) * mm});
            skLineSegment(sketch, "E636", {"start": v(-67.42, 47.98) * mm, "end": v(-67.2, 47.16) * mm});
            skLineSegment(sketch, "E637", {"start": v(-67.2, 47.16) * mm, "end": v(-65.86, 46.72) * mm});
            skLineSegment(sketch, "E638", {"start": v(-65.86, 46.72) * mm, "end": v(-66.57, 47.93) * mm});
            skLineSegment(sketch, "E639", {"start": v(-66.57, 47.93) * mm, "end": v(-67.42, 47.98) * mm});
            skLineSegment(sketch, "E640", {"start": v(-62.18, 49.4) * mm, "end": v(-61.96, 48.57) * mm});
            skLineSegment(sketch, "E641", {"start": v(-61.96, 48.57) * mm, "end": v(-62.9, 47.52) * mm});
            skLineSegment(sketch, "E642", {"start": v(-62.9, 47.52) * mm, "end": v(-62.9, 48.93) * mm});
            skLineSegment(sketch, "E643", {"start": v(-62.9, 48.93) * mm, "end": v(-62.18, 49.4) * mm});
            skLineSegment(sketch, "E644", {"start": v(-62.62, 40.62) * mm, "end": v(-62.32, 41.42) * mm});
            skLineSegment(sketch, "E645", {"start": v(-62.32, 41.42) * mm, "end": v(-63.14, 42.55) * mm});
            skLineSegment(sketch, "E646", {"start": v(-63.14, 42.55) * mm, "end": v(-63.29, 41.16) * mm});
            skLineSegment(sketch, "E647", {"start": v(-63.29, 41.16) * mm, "end": v(-62.62, 40.62) * mm});
            skLineSegment(sketch, "E648", {"start": v(-59.21, 44.84) * mm, "end": v(-59.88, 45.38) * mm});
            skLineSegment(sketch, "E649", {"start": v(-59.88, 45.38) * mm, "end": v(-61.21, 44.95) * mm});
            skLineSegment(sketch, "E650", {"start": v(-61.21, 44.95) * mm, "end": v(-59.93, 44.38) * mm});
            skLineSegment(sketch, "E651", {"start": v(-59.93, 44.38) * mm, "end": v(-59.21, 44.84) * mm});
            skLineSegment(sketch, "E652", {"start": v(-67.7, 42.56) * mm, "end": v(-66.84, 42.52) * mm});
            skLineSegment(sketch, "E653", {"start": v(-66.84, 42.52) * mm, "end": v(-66.02, 43.65) * mm});
            skLineSegment(sketch, "E654", {"start": v(-66.02, 43.65) * mm, "end": v(-67.39, 43.35) * mm});
            skLineSegment(sketch, "E655", {"start": v(-67.39, 43.35) * mm, "end": v(-67.7, 42.56) * mm});
            skLineSegment(sketch, "E656", {"start": v(-61.57, 33.86) * mm, "end": v(-60.9, 31.4) * mm});
            skLineSegment(sketch, "E657", {"start": v(-60.9, 31.4) * mm, "end": v(-57.61, 30.33) * mm});
            skLineSegment(sketch, "E658", {"start": v(-57.28, 30.74) * mm, "end": v(-59.01, 33.73) * mm});
            skLineSegment(sketch, "E659", {"start": v(-59.01, 33.73) * mm, "end": v(-61.57, 33.86) * mm});
            skLineSegment(sketch, "E660", {"start": v(-61.93, 26.82) * mm, "end": v(-59.37, 26.7) * mm});
            skLineSegment(sketch, "E661", {"start": v(-59.37, 26.7) * mm, "end": v(-57.34, 29.49) * mm});
            skLineSegment(sketch, "E662", {"start": v(-57.63, 29.93) * mm, "end": v(-61, 29.2) * mm});
            skLineSegment(sketch, "E663", {"start": v(-61, 29.2) * mm, "end": v(-61.93, 26.82) * mm});
            skLineSegment(sketch, "E664", {"start": v(-55.34, 24.3) * mm, "end": v(-54.43, 26.7) * mm});
            skLineSegment(sketch, "E665", {"start": v(-54.43, 26.7) * mm, "end": v(-56.46, 29.49) * mm});
            skLineSegment(sketch, "E666", {"start": v(-56.98, 29.35) * mm, "end": v(-57.33, 25.91) * mm});
            skLineSegment(sketch, "E667", {"start": v(-57.33, 25.91) * mm, "end": v(-55.34, 24.3) * mm});
            skLineSegment(sketch, "E668", {"start": v(-56.21, 29.8) * mm, "end": v(-53.05, 28.4) * mm});
            skLineSegment(sketch, "E669", {"start": v(-53.05, 28.4) * mm, "end": v(-50.9, 29.79) * mm});
            skLineSegment(sketch, "E670", {"start": v(-56.19, 30.33) * mm, "end": v(-52.9, 31.4) * mm});
            skLineSegment(sketch, "E671", {"start": v(-52.9, 31.4) * mm, "end": v(-50.9, 29.79) * mm});
            skLineSegment(sketch, "E672", {"start": v(-54.76, 35.7) * mm, "end": v(-54.1, 33.23) * mm});
            skLineSegment(sketch, "E673", {"start": v(-54.1, 33.23) * mm, "end": v(-56.4, 30.65) * mm});
            skLineSegment(sketch, "E674", {"start": v(-56.9, 30.84) * mm, "end": v(-56.9, 34.3) * mm});
            skLineSegment(sketch, "E675", {"start": v(-56.9, 34.3) * mm, "end": v(-54.76, 35.7) * mm});
            skArc(sketch, "E676", {"start": v(-57.34, 29.49) * mm, "mid": v(-57.17, 29.4) * mm, "end": v(-56.98, 29.35) * mm});
            skArc(sketch, "E677.trimOffspring", {"start": v(-57.61, 30.33) * mm, "mid": v(-57.65, 30.13) * mm, "end": v(-57.63, 29.93) * mm});
            skArc(sketch, "E678.trimOffspring", {"start": v(-56.9, 30.84) * mm, "mid": v(-57.1, 30.82) * mm, "end": v(-57.28, 30.74) * mm});
            skArc(sketch, "E679.trimOffspring", {"start": v(-56.19, 30.33) * mm, "mid": v(-56.27, 30.5) * mm, "end": v(-56.4, 30.65) * mm});
            skArc(sketch, "E680.trimOffspring", {"start": v(-56.46, 29.49) * mm, "mid": v(-56.32, 29.62) * mm, "end": v(-56.21, 29.8) * mm});
            skLineSegment(sketch, "E681", {"start": v(-60.5, 33) * mm, "end": v(-60.27, 32.17) * mm});
            skLineSegment(sketch, "E682", {"start": v(-60.27, 32.17) * mm, "end": v(-58.94, 31.74) * mm});
            skLineSegment(sketch, "E683", {"start": v(-58.94, 31.74) * mm, "end": v(-59.64, 32.95) * mm});
            skLineSegment(sketch, "E684", {"start": v(-59.64, 32.95) * mm, "end": v(-60.5, 33) * mm});
            skLineSegment(sketch, "E685", {"start": v(-55.25, 34.4) * mm, "end": v(-55.03, 33.58) * mm});
            skLineSegment(sketch, "E686", {"start": v(-55.03, 33.58) * mm, "end": v(-55.97, 32.54) * mm});
            skLineSegment(sketch, "E687", {"start": v(-55.97, 32.54) * mm, "end": v(-55.97, 33.94) * mm});
            skLineSegment(sketch, "E688", {"start": v(-55.97, 33.94) * mm, "end": v(-55.25, 34.4) * mm});
            skLineSegment(sketch, "E689", {"start": v(-55.7, 25.63) * mm, "end": v(-55.4, 26.43) * mm});
            skLineSegment(sketch, "E690", {"start": v(-55.4, 26.43) * mm, "end": v(-56.22, 27.57) * mm});
            skLineSegment(sketch, "E691", {"start": v(-56.22, 27.57) * mm, "end": v(-56.36, 26.17) * mm});
            skLineSegment(sketch, "E692", {"start": v(-56.36, 26.17) * mm, "end": v(-55.7, 25.63) * mm});
            skLineSegment(sketch, "E693", {"start": v(-52.29, 29.86) * mm, "end": v(-52.95, 30.4) * mm});
            skLineSegment(sketch, "E694", {"start": v(-52.95, 30.4) * mm, "end": v(-54.29, 29.96) * mm});
            skLineSegment(sketch, "E695", {"start": v(-54.29, 29.96) * mm, "end": v(-53, 29.4) * mm});
            skLineSegment(sketch, "E696", {"start": v(-53, 29.4) * mm, "end": v(-52.29, 29.86) * mm});
            skLineSegment(sketch, "E697", {"start": v(-60.77, 27.57) * mm, "end": v(-59.92, 27.53) * mm});
            skLineSegment(sketch, "E698", {"start": v(-59.92, 27.53) * mm, "end": v(-59.1, 28.66) * mm});
            skLineSegment(sketch, "E699", {"start": v(-59.1, 28.66) * mm, "end": v(-60.46, 28.37) * mm});
            skLineSegment(sketch, "E700", {"start": v(-60.46, 28.37) * mm, "end": v(-60.77, 27.57) * mm});
            skLineSegment(sketch, "E701", {"start": v(-75.47, 17.7) * mm, "end": v(-74.8, 15.24) * mm});
            skLineSegment(sketch, "E702", {"start": v(-74.8, 15.24) * mm, "end": v(-71.51, 14.17) * mm});
            skLineSegment(sketch, "E703", {"start": v(-71.17, 14.58) * mm, "end": v(-72.91, 17.57) * mm});
            skLineSegment(sketch, "E704", {"start": v(-72.91, 17.57) * mm, "end": v(-75.47, 17.7) * mm});
            skLineSegment(sketch, "E705", {"start": v(-75.82, 10.66) * mm, "end": v(-73.27, 10.54) * mm});
            skLineSegment(sketch, "E706", {"start": v(-73.27, 10.54) * mm, "end": v(-71.24, 13.33) * mm});
            skLineSegment(sketch, "E707", {"start": v(-71.53, 13.78) * mm, "end": v(-74.9, 13.05) * mm});
            skLineSegment(sketch, "E708", {"start": v(-74.9, 13.05) * mm, "end": v(-75.82, 10.66) * mm});
            skLineSegment(sketch, "E709", {"start": v(-69.24, 8.14) * mm, "end": v(-68.33, 10.54) * mm});
            skLineSegment(sketch, "E710", {"start": v(-68.33, 10.54) * mm, "end": v(-70.36, 13.33) * mm});
            skLineSegment(sketch, "E711", {"start": v(-70.87, 13.2) * mm, "end": v(-71.22, 9.75) * mm});
            skLineSegment(sketch, "E712", {"start": v(-71.22, 9.75) * mm, "end": v(-69.24, 8.14) * mm});
            skLineSegment(sketch, "E713", {"start": v(-70.11, 13.63) * mm, "end": v(-66.95, 12.24) * mm});
            skLineSegment(sketch, "E714", {"start": v(-66.95, 12.24) * mm, "end": v(-64.8, 13.63) * mm});
            skLineSegment(sketch, "E715", {"start": v(-70.08, 14.17) * mm, "end": v(-66.8, 15.24) * mm});
            skLineSegment(sketch, "E716", {"start": v(-66.8, 15.24) * mm, "end": v(-64.8, 13.63) * mm});
            skLineSegment(sketch, "E717", {"start": v(-68.66, 19.54) * mm, "end": v(-68, 17.07) * mm});
            skLineSegment(sketch, "E718", {"start": v(-68, 17.07) * mm, "end": v(-70.3, 14.5) * mm});
            skLineSegment(sketch, "E719", {"start": v(-70.8, 14.69) * mm, "end": v(-70.8, 18.14) * mm});
            skLineSegment(sketch, "E720", {"start": v(-70.8, 18.14) * mm, "end": v(-68.66, 19.54) * mm});
            skArc(sketch, "E721", {"start": v(-71.24, 13.33) * mm, "mid": v(-71.07, 13.24) * mm, "end": v(-70.87, 13.2) * mm});
            skArc(sketch, "E722.trimOffspring", {"start": v(-71.51, 14.17) * mm, "mid": v(-71.55, 13.97) * mm, "end": v(-71.53, 13.78) * mm});
            skArc(sketch, "E723.trimOffspring", {"start": v(-70.8, 14.69) * mm, "mid": v(-71, 14.66) * mm, "end": v(-71.17, 14.58) * mm});
            skArc(sketch, "E724.trimOffspring", {"start": v(-70.08, 14.17) * mm, "mid": v(-70.17, 14.35) * mm, "end": v(-70.3, 14.5) * mm});
            skArc(sketch, "E725.trimOffspring", {"start": v(-70.36, 13.33) * mm, "mid": v(-70.21, 13.47) * mm, "end": v(-70.11, 13.63) * mm});
            skLineSegment(sketch, "E726", {"start": v(-74.4, 16.84) * mm, "end": v(-74.17, 16.01) * mm});
            skLineSegment(sketch, "E727", {"start": v(-74.17, 16.01) * mm, "end": v(-72.84, 15.58) * mm});
            skLineSegment(sketch, "E728", {"start": v(-72.84, 15.58) * mm, "end": v(-73.54, 16.8) * mm});
            skLineSegment(sketch, "E729", {"start": v(-73.54, 16.8) * mm, "end": v(-74.4, 16.84) * mm});
            skLineSegment(sketch, "E730", {"start": v(-69.15, 18.25) * mm, "end": v(-68.93, 17.43) * mm});
            skLineSegment(sketch, "E731", {"start": v(-68.93, 17.43) * mm, "end": v(-69.86, 16.38) * mm});
            skLineSegment(sketch, "E732", {"start": v(-69.86, 16.38) * mm, "end": v(-69.86, 17.78) * mm});
            skLineSegment(sketch, "E733", {"start": v(-69.86, 17.78) * mm, "end": v(-69.15, 18.25) * mm});
            skLineSegment(sketch, "E734", {"start": v(-69.6, 9.48) * mm, "end": v(-69.3, 10.28) * mm});
            skLineSegment(sketch, "E735", {"start": v(-69.3, 10.28) * mm, "end": v(-70.12, 11.4) * mm});
            skLineSegment(sketch, "E736", {"start": v(-70.12, 11.4) * mm, "end": v(-70.26, 10.01) * mm});
            skLineSegment(sketch, "E737", {"start": v(-70.26, 10.01) * mm, "end": v(-69.6, 9.48) * mm});
            skLineSegment(sketch, "E738", {"start": v(-66.18, 13.7) * mm, "end": v(-66.85, 14.24) * mm});
            skLineSegment(sketch, "E739", {"start": v(-66.85, 14.24) * mm, "end": v(-68.18, 13.8) * mm});
            skLineSegment(sketch, "E740", {"start": v(-68.18, 13.8) * mm, "end": v(-66.9, 13.24) * mm});
            skLineSegment(sketch, "E741", {"start": v(-66.9, 13.24) * mm, "end": v(-66.18, 13.7) * mm});
            skLineSegment(sketch, "E742", {"start": v(-74.67, 11.42) * mm, "end": v(-73.81, 11.37) * mm});
            skLineSegment(sketch, "E743", {"start": v(-73.81, 11.37) * mm, "end": v(-73, 12.5) * mm});
            skLineSegment(sketch, "E744", {"start": v(-73, 12.5) * mm, "end": v(-74.36, 12.21) * mm});
            skLineSegment(sketch, "E745", {"start": v(-74.36, 12.21) * mm, "end": v(-74.67, 11.42) * mm});
            skLineSegment(sketch, "E746", {"start": v(-84.08, -2.92) * mm, "end": v(-82.11, -4.56) * mm});
            skLineSegment(sketch, "E747", {"start": v(-82.11, -4.56) * mm, "end": v(-78.8, -3.55) * mm});
            skLineSegment(sketch, "E748", {"start": v(-78.77, -3.01) * mm, "end": v(-81.9, -1.56) * mm});
            skLineSegment(sketch, "E749", {"start": v(-81.9, -1.56) * mm, "end": v(-84.08, -2.92) * mm});
            skLineSegment(sketch, "E750", {"start": v(-80.33, -8.9) * mm, "end": v(-78.16, -7.53) * mm});
            skLineSegment(sketch, "E751", {"start": v(-78.16, -7.53) * mm, "end": v(-78.1, -4.08) * mm});
            skLineSegment(sketch, "E752", {"start": v(-78.6, -3.88) * mm, "end": v(-80.95, -6.41) * mm});
            skLineSegment(sketch, "E753", {"start": v(-80.95, -6.41) * mm, "end": v(-80.33, -8.9) * mm});
            skLineSegment(sketch, "E754", {"start": v(-73.49, -7.18) * mm, "end": v(-74.12, -4.7) * mm});
            skLineSegment(sketch, "E755", {"start": v(-74.12, -4.7) * mm, "end": v(-77.38, -3.57) * mm});
            skLineSegment(sketch, "E756", {"start": v(-77.72, -3.98) * mm, "end": v(-76.04, -7) * mm});
            skLineSegment(sketch, "E757", {"start": v(-76.04, -7) * mm, "end": v(-73.49, -7.18) * mm});
            skLineSegment(sketch, "E758", {"start": v(-77.36, -3.18) * mm, "end": v(-73.97, -2.51) * mm});
            skLineSegment(sketch, "E759", {"start": v(-73.97, -2.51) * mm, "end": v(-73, -0.14) * mm});
            skLineSegment(sketch, "E760", {"start": v(-77.64, -2.73) * mm, "end": v(-75.56, 0.03) * mm});
            skLineSegment(sketch, "E761", {"start": v(-75.56, 0.03) * mm, "end": v(-73, -0.14) * mm});
            skLineSegment(sketch, "E762", {"start": v(-79.55, 2.5) * mm, "end": v(-77.6, 0.85) * mm});
            skLineSegment(sketch, "E763", {"start": v(-77.6, 0.85) * mm, "end": v(-78, -2.58) * mm});
            skLineSegment(sketch, "E764", {"start": v(-78.52, -2.71) * mm, "end": v(-80.5, 0.12) * mm});
            skLineSegment(sketch, "E765", {"start": v(-80.5, 0.12) * mm, "end": v(-79.55, 2.5) * mm});
            skArc(sketch, "E766", {"start": v(-78.1, -4.08) * mm, "mid": v(-77.9, -4.05) * mm, "end": v(-77.72, -3.98) * mm});
            skArc(sketch, "E767.trimOffspring", {"start": v(-78.8, -3.55) * mm, "mid": v(-78.73, -3.73) * mm, "end": v(-78.6, -3.88) * mm});
            skArc(sketch, "E768.trimOffspring", {"start": v(-78.52, -2.71) * mm, "mid": v(-78.67, -2.85) * mm, "end": v(-78.77, -3.01) * mm});
            skArc(sketch, "E769.trimOffspring", {"start": v(-77.64, -2.73) * mm, "mid": v(-77.81, -2.63) * mm, "end": v(-78, -2.58) * mm});
            skArc(sketch, "E770.trimOffspring", {"start": v(-77.38, -3.57) * mm, "mid": v(-77.34, -3.38) * mm, "end": v(-77.36, -3.18) * mm});
            skLineSegment(sketch, "E771", {"start": v(-82.7, -3.01) * mm, "end": v(-82.04, -3.56) * mm});
            skLineSegment(sketch, "E772", {"start": v(-82.04, -3.56) * mm, "end": v(-80.7, -3.15) * mm});
            skLineSegment(sketch, "E773", {"start": v(-80.7, -3.15) * mm, "end": v(-81.97, -2.56) * mm});
            skLineSegment(sketch, "E774", {"start": v(-81.97, -2.56) * mm, "end": v(-82.7, -3.01) * mm});
            skLineSegment(sketch, "E775", {"start": v(-79.22, 1.15) * mm, "end": v(-78.56, 0.6) * mm});
            skLineSegment(sketch, "E776", {"start": v(-78.56, 0.6) * mm, "end": v(-78.73, -0.79) * mm});
            skLineSegment(sketch, "E777", {"start": v(-78.73, -0.79) * mm, "end": v(-79.53, 0.36) * mm});
            skLineSegment(sketch, "E778", {"start": v(-79.53, 0.36) * mm, "end": v(-79.22, 1.15) * mm});
            skLineSegment(sketch, "E779", {"start": v(-74.55, -6.29) * mm, "end": v(-74.76, -5.46) * mm});
            skLineSegment(sketch, "E780", {"start": v(-74.76, -5.46) * mm, "end": v(-76.08, -5) * mm});
            skLineSegment(sketch, "E781", {"start": v(-76.08, -5) * mm, "end": v(-75.4, -6.23) * mm});
            skLineSegment(sketch, "E782", {"start": v(-75.4, -6.23) * mm, "end": v(-74.55, -6.29) * mm});
            skLineSegment(sketch, "E783", {"start": v(-74.18, -0.87) * mm, "end": v(-75.03, -0.82) * mm});
            skLineSegment(sketch, "E784", {"start": v(-75.03, -0.82) * mm, "end": v(-75.87, -1.94) * mm});
            skLineSegment(sketch, "E785", {"start": v(-75.87, -1.94) * mm, "end": v(-74.5, -1.66) * mm});
            skLineSegment(sketch, "E786", {"start": v(-74.5, -1.66) * mm, "end": v(-74.18, -0.87) * mm});
            skLineSegment(sketch, "E787", {"start": v(-79.81, -7.61) * mm, "end": v(-79.1, -7.16) * mm});
            skLineSegment(sketch, "E788", {"start": v(-79.1, -7.16) * mm, "end": v(-79.07, -5.76) * mm});
            skLineSegment(sketch, "E789", {"start": v(-79.07, -5.76) * mm, "end": v(-80.02, -6.78) * mm});
            skLineSegment(sketch, "E790", {"start": v(-80.02, -6.78) * mm, "end": v(-79.81, -7.61) * mm});
            skLineSegment(sketch, "E791", {"start": v(-70.18, -16.22) * mm, "end": v(-69.5, -18.7) * mm});
            skLineSegment(sketch, "E792", {"start": v(-69.5, -18.7) * mm, "end": v(-66.22, -19.76) * mm});
            skLineSegment(sketch, "E793", {"start": v(-65.89, -19.34) * mm, "end": v(-67.63, -16.36) * mm});
            skLineSegment(sketch, "E794", {"start": v(-67.63, -16.36) * mm, "end": v(-70.18, -16.22) * mm});
            skLineSegment(sketch, "E795", {"start": v(-70.54, -23.27) * mm, "end": v(-67.98, -23.4) * mm});
            skLineSegment(sketch, "E796", {"start": v(-67.98, -23.4) * mm, "end": v(-65.95, -20.6) * mm});
            skLineSegment(sketch, "E797", {"start": v(-66.24, -20.15) * mm, "end": v(-69.62, -20.88) * mm});
            skLineSegment(sketch, "E798", {"start": v(-69.62, -20.88) * mm, "end": v(-70.54, -23.27) * mm});
            skLineSegment(sketch, "E799", {"start": v(-63.95, -25.79) * mm, "end": v(-63.04, -23.4) * mm});
            skLineSegment(sketch, "E800", {"start": v(-63.04, -23.4) * mm, "end": v(-65.07, -20.6) * mm});
            skLineSegment(sketch, "E801", {"start": v(-65.59, -20.74) * mm, "end": v(-65.94, -24.17) * mm});
            skLineSegment(sketch, "E802", {"start": v(-65.94, -24.17) * mm, "end": v(-63.95, -25.79) * mm});
            skLineSegment(sketch, "E803", {"start": v(-64.83, -20.3) * mm, "end": v(-61.67, -21.69) * mm});
            skLineSegment(sketch, "E804", {"start": v(-61.67, -21.69) * mm, "end": v(-59.52, -20.3) * mm});
            skLineSegment(sketch, "E805", {"start": v(-64.8, -19.76) * mm, "end": v(-61.51, -18.7) * mm});
            skLineSegment(sketch, "E806", {"start": v(-61.51, -18.7) * mm, "end": v(-59.52, -20.3) * mm});
            skLineSegment(sketch, "E807", {"start": v(-63.37, -14.39) * mm, "end": v(-62.7, -16.86) * mm});
            skLineSegment(sketch, "E808", {"start": v(-62.7, -16.86) * mm, "end": v(-65.01, -19.43) * mm});
            skLineSegment(sketch, "E809", {"start": v(-65.51, -19.24) * mm, "end": v(-65.51, -15.79) * mm});
            skLineSegment(sketch, "E810", {"start": v(-65.51, -15.79) * mm, "end": v(-63.37, -14.39) * mm});
            skArc(sketch, "E811", {"start": v(-65.95, -20.6) * mm, "mid": v(-65.78, -20.7) * mm, "end": v(-65.59, -20.74) * mm});
            skArc(sketch, "E812.trimOffspring", {"start": v(-66.22, -19.76) * mm, "mid": v(-66.26, -19.95) * mm, "end": v(-66.24, -20.15) * mm});
            skArc(sketch, "E813.trimOffspring", {"start": v(-65.51, -19.24) * mm, "mid": v(-65.7, -19.27) * mm, "end": v(-65.89, -19.34) * mm});
            skArc(sketch, "E814.trimOffspring", {"start": v(-64.8, -19.76) * mm, "mid": v(-64.88, -19.58) * mm, "end": v(-65.01, -19.43) * mm});
            skArc(sketch, "E815.trimOffspring", {"start": v(-65.07, -20.6) * mm, "mid": v(-64.93, -20.46) * mm, "end": v(-64.83, -20.3) * mm});
            skLineSegment(sketch, "E816", {"start": v(-69.1, -17.1) * mm, "end": v(-68.88, -17.91) * mm});
            skLineSegment(sketch, "E817", {"start": v(-68.88, -17.91) * mm, "end": v(-67.55, -18.35) * mm});
            skLineSegment(sketch, "E818", {"start": v(-67.55, -18.35) * mm, "end": v(-68.25, -17.14) * mm});
            skLineSegment(sketch, "E819", {"start": v(-68.25, -17.14) * mm, "end": v(-69.1, -17.1) * mm});
            skLineSegment(sketch, "E820", {"start": v(-63.86, -15.68) * mm, "end": v(-63.64, -16.5) * mm});
            skLineSegment(sketch, "E821", {"start": v(-63.64, -16.5) * mm, "end": v(-64.58, -17.55) * mm});
            skLineSegment(sketch, "E822", {"start": v(-64.58, -17.55) * mm, "end": v(-64.58, -16.15) * mm});
            skLineSegment(sketch, "E823", {"start": v(-64.58, -16.15) * mm, "end": v(-63.86, -15.68) * mm});
            skLineSegment(sketch, "E824", {"start": v(-64.3, -24.45) * mm, "end": v(-64, -23.65) * mm});
            skLineSegment(sketch, "E825", {"start": v(-64, -23.65) * mm, "end": v(-64.83, -22.52) * mm});
            skLineSegment(sketch, "E826", {"start": v(-64.83, -22.52) * mm, "end": v(-64.97, -23.91) * mm});
            skLineSegment(sketch, "E827", {"start": v(-64.97, -23.91) * mm, "end": v(-64.3, -24.45) * mm});
            skLineSegment(sketch, "E828", {"start": v(-60.9, -20.23) * mm, "end": v(-61.56, -19.7) * mm});
            skLineSegment(sketch, "E829", {"start": v(-61.56, -19.7) * mm, "end": v(-62.9, -20.12) * mm});
            skLineSegment(sketch, "E830", {"start": v(-62.9, -20.12) * mm, "end": v(-61.61, -20.7) * mm});
            skLineSegment(sketch, "E831", {"start": v(-61.61, -20.7) * mm, "end": v(-60.9, -20.23) * mm});
            skLineSegment(sketch, "E832", {"start": v(-69.38, -22.51) * mm, "end": v(-68.53, -22.56) * mm});
            skLineSegment(sketch, "E833", {"start": v(-68.53, -22.56) * mm, "end": v(-67.7, -21.42) * mm});
            skLineSegment(sketch, "E834", {"start": v(-67.7, -21.42) * mm, "end": v(-69.07, -21.72) * mm});
            skLineSegment(sketch, "E835", {"start": v(-69.07, -21.72) * mm, "end": v(-69.38, -22.51) * mm});
            skLineSegment(sketch, "E836", {"start": v(-63.33, -31.16) * mm, "end": v(-63.76, -33.68) * mm});
            skLineSegment(sketch, "E837", {"start": v(-63.76, -33.68) * mm, "end": v(-61.23, -36.04) * mm});
            skLineSegment(sketch, "E838", {"start": v(-60.75, -35.8) * mm, "end": v(-61.07, -32.36) * mm});
            skLineSegment(sketch, "E839", {"start": v(-61.07, -32.36) * mm, "end": v(-63.33, -31.16) * mm});
            skLineSegment(sketch, "E840", {"start": v(-66.63, -37.4) * mm, "end": v(-64.36, -38.59) * mm});
            skLineSegment(sketch, "E841", {"start": v(-64.36, -38.59) * mm, "end": v(-61.34, -36.91) * mm});
            skLineSegment(sketch, "E842", {"start": v(-61.42, -36.38) * mm, "end": v(-64.79, -35.62) * mm});
            skLineSegment(sketch, "E843", {"start": v(-64.79, -35.62) * mm, "end": v(-66.63, -37.4) * mm});
            skLineSegment(sketch, "E844", {"start": v(-61.72, -42.46) * mm, "end": v(-59.88, -40.68) * mm});
            skLineSegment(sketch, "E845", {"start": v(-59.88, -40.68) * mm, "end": v(-60.54, -37.29) * mm});
            skLineSegment(sketch, "E846", {"start": v(-61.07, -37.2) * mm, "end": v(-62.84, -40.16) * mm});
            skLineSegment(sketch, "E847", {"start": v(-62.84, -40.16) * mm, "end": v(-61.72, -42.46) * mm});
            skLineSegment(sketch, "E848", {"start": v(-60.2, -37.11) * mm, "end": v(-57.92, -39.71) * mm});
            skLineSegment(sketch, "E849", {"start": v(-57.92, -39.71) * mm, "end": v(-55.38, -39.36) * mm});
            skLineSegment(sketch, "E850", {"start": v(-59.94, -36.64) * mm, "end": v(-56.51, -37.06) * mm});
            skLineSegment(sketch, "E851", {"start": v(-56.51, -37.06) * mm, "end": v(-55.38, -39.36) * mm});
            skLineSegment(sketch, "E852", {"start": v(-56.38, -32.37) * mm, "end": v(-56.82, -34.9) * mm});
            skLineSegment(sketch, "E853", {"start": v(-56.82, -34.9) * mm, "end": v(-60, -36.25) * mm});
            skLineSegment(sketch, "E854", {"start": v(-60.37, -35.87) * mm, "end": v(-58.9, -32.74) * mm});
            skLineSegment(sketch, "E855", {"start": v(-58.9, -32.74) * mm, "end": v(-56.38, -32.37) * mm});
            skArc(sketch, "E856", {"start": v(-61.34, -36.91) * mm, "mid": v(-61.23, -37.07) * mm, "end": v(-61.07, -37.2) * mm});
            skArc(sketch, "E857.trimOffspring", {"start": v(-61.23, -36.04) * mm, "mid": v(-61.35, -36.2) * mm, "end": v(-61.42, -36.38) * mm});
            skArc(sketch, "E858.trimOffspring", {"start": v(-60.37, -35.87) * mm, "mid": v(-60.56, -35.81) * mm, "end": v(-60.75, -35.8) * mm});
            skArc(sketch, "E859.trimOffspring", {"start": v(-59.94, -36.64) * mm, "mid": v(-59.94, -36.44) * mm, "end": v(-60, -36.25) * mm});
            skArc(sketch, "E860.trimOffspring", {"start": v(-60.54, -37.29) * mm, "mid": v(-60.36, -37.22) * mm, "end": v(-60.2, -37.11) * mm});
            skLineSegment(sketch, "E861", {"start": v(-62.72, -32.4) * mm, "end": v(-62.86, -33.24) * mm});
            skLineSegment(sketch, "E862", {"start": v(-62.86, -33.24) * mm, "end": v(-61.84, -34.2) * mm});
            skLineSegment(sketch, "E863", {"start": v(-61.84, -34.2) * mm, "end": v(-61.96, -32.8) * mm});
            skLineSegment(sketch, "E864", {"start": v(-61.96, -32.8) * mm, "end": v(-62.72, -32.4) * mm});
            skLineSegment(sketch, "E865", {"start": v(-57.37, -33.34) * mm, "end": v(-57.52, -34.18) * mm});
            skLineSegment(sketch, "E866", {"start": v(-57.52, -34.18) * mm, "end": v(-58.8, -34.73) * mm});
            skLineSegment(sketch, "E867", {"start": v(-58.8, -34.73) * mm, "end": v(-58.21, -33.46) * mm});
            skLineSegment(sketch, "E868", {"start": v(-58.21, -33.46) * mm, "end": v(-57.37, -33.34) * mm});
            skLineSegment(sketch, "E869", {"start": v(-61.48, -41.1) * mm, "end": v(-60.87, -40.5) * mm});
            skLineSegment(sketch, "E870", {"start": v(-60.87, -40.5) * mm, "end": v(-61.14, -39.13) * mm});
            skLineSegment(sketch, "E871", {"start": v(-61.14, -39.13) * mm, "end": v(-61.85, -40.33) * mm});
            skLineSegment(sketch, "E872", {"start": v(-61.85, -40.33) * mm, "end": v(-61.48, -41.1) * mm});
            skLineSegment(sketch, "E873", {"start": v(-56.6, -38.71) * mm, "end": v(-56.98, -37.94) * mm});
            skLineSegment(sketch, "E874", {"start": v(-56.98, -37.94) * mm, "end": v(-58.37, -37.77) * mm});
            skLineSegment(sketch, "E875", {"start": v(-58.37, -37.77) * mm, "end": v(-57.45, -38.83) * mm});
            skLineSegment(sketch, "E876", {"start": v(-57.45, -38.83) * mm, "end": v(-56.6, -38.71) * mm});
            skLineSegment(sketch, "E877", {"start": v(-65.26, -37.2) * mm, "end": v(-64.5, -37.6) * mm});
            skLineSegment(sketch, "E878", {"start": v(-64.5, -37.6) * mm, "end": v(-63.28, -36.92) * mm});
            skLineSegment(sketch, "E879", {"start": v(-63.28, -36.92) * mm, "end": v(-64.64, -36.6) * mm});
            skLineSegment(sketch, "E880", {"start": v(-64.64, -36.6) * mm, "end": v(-65.26, -37.2) * mm});
            skLineSegment(sketch, "E881", {"start": v(18.85, 38.52) * mm, "end": v(19.52, 36.05) * mm});
            skLineSegment(sketch, "E882", {"start": v(19.52, 36.05) * mm, "end": v(22.8, 34.98) * mm});
            skLineSegment(sketch, "E883", {"start": v(23.14, 35.4) * mm, "end": v(21.4, 38.38) * mm});
            skLineSegment(sketch, "E884", {"start": v(21.4, 38.38) * mm, "end": v(18.85, 38.52) * mm});
            skLineSegment(sketch, "E885", {"start": v(18.5, 31.47) * mm, "end": v(21.05, 31.35) * mm});
            skLineSegment(sketch, "E886", {"start": v(21.05, 31.35) * mm, "end": v(23.08, 34.14) * mm});
            skLineSegment(sketch, "E887", {"start": v(22.79, 34.6) * mm, "end": v(19.41, 33.86) * mm});
            skLineSegment(sketch, "E888", {"start": v(19.41, 33.86) * mm, "end": v(18.5, 31.47) * mm});
            skLineSegment(sketch, "E889", {"start": v(25.08, 28.96) * mm, "end": v(26, 31.35) * mm});
            skLineSegment(sketch, "E890", {"start": v(26, 31.35) * mm, "end": v(23.96, 34.14) * mm});
            skLineSegment(sketch, "E891", {"start": v(23.45, 34) * mm, "end": v(23.1, 30.57) * mm});
            skLineSegment(sketch, "E892", {"start": v(23.1, 30.57) * mm, "end": v(25.08, 28.96) * mm});
            skLineSegment(sketch, "E893", {"start": v(24.2, 34.45) * mm, "end": v(27.37, 33.05) * mm});
            skLineSegment(sketch, "E894", {"start": v(27.37, 33.05) * mm, "end": v(29.51, 34.45) * mm});
            skLineSegment(sketch, "E895", {"start": v(24.23, 34.98) * mm, "end": v(27.52, 36.05) * mm});
            skLineSegment(sketch, "E896", {"start": v(27.52, 36.05) * mm, "end": v(29.51, 34.45) * mm});
            skLineSegment(sketch, "E897", {"start": v(25.66, 40.35) * mm, "end": v(26.32, 37.88) * mm});
            skLineSegment(sketch, "E898", {"start": v(26.32, 37.88) * mm, "end": v(24.02, 35.3) * mm});
            skLineSegment(sketch, "E899", {"start": v(23.52, 35.5) * mm, "end": v(23.52, 38.95) * mm});
            skLineSegment(sketch, "E900", {"start": v(23.52, 38.95) * mm, "end": v(25.66, 40.35) * mm});
            skArc(sketch, "E901", {"start": v(23.08, 34.14) * mm, "mid": v(23.25, 34.05) * mm, "end": v(23.45, 34) * mm});
            skArc(sketch, "E902.trimOffspring", {"start": v(22.8, 34.98) * mm, "mid": v(22.77, 34.79) * mm, "end": v(22.79, 34.6) * mm});
            skArc(sketch, "E903.trimOffspring", {"start": v(23.52, 35.5) * mm, "mid": v(23.33, 35.47) * mm, "end": v(23.14, 35.4) * mm});
            skArc(sketch, "E904.trimOffspring", {"start": v(24.23, 34.98) * mm, "mid": v(24.15, 35.16) * mm, "end": v(24.02, 35.3) * mm});
            skArc(sketch, "E905.trimOffspring", {"start": v(23.96, 34.14) * mm, "mid": v(24.1, 34.28) * mm, "end": v(24.2, 34.45) * mm});
            skLineSegment(sketch, "E906", {"start": v(19.93, 37.65) * mm, "end": v(20.15, 36.83) * mm});
            skLineSegment(sketch, "E907", {"start": v(20.15, 36.83) * mm, "end": v(21.48, 36.4) * mm});
            skLineSegment(sketch, "E908", {"start": v(21.48, 36.4) * mm, "end": v(20.78, 37.6) * mm});
            skLineSegment(sketch, "E909", {"start": v(20.78, 37.6) * mm, "end": v(19.93, 37.65) * mm});
            skLineSegment(sketch, "E910", {"start": v(25.17, 39.06) * mm, "end": v(25.39, 38.24) * mm});
            skLineSegment(sketch, "E911", {"start": v(25.39, 38.24) * mm, "end": v(24.46, 37.2) * mm});
            skLineSegment(sketch, "E912", {"start": v(24.46, 37.2) * mm, "end": v(24.46, 38.6) * mm});
            skLineSegment(sketch, "E913", {"start": v(24.46, 38.6) * mm, "end": v(25.17, 39.06) * mm});
            skLineSegment(sketch, "E914", {"start": v(24.72, 30.3) * mm, "end": v(25.03, 31.09) * mm});
            skLineSegment(sketch, "E915", {"start": v(25.03, 31.09) * mm, "end": v(24.2, 32.22) * mm});
            skLineSegment(sketch, "E916", {"start": v(24.2, 32.22) * mm, "end": v(24.06, 30.83) * mm});
            skLineSegment(sketch, "E917", {"start": v(24.06, 30.83) * mm, "end": v(24.72, 30.3) * mm});
            skLineSegment(sketch, "E918", {"start": v(28.13, 34.52) * mm, "end": v(27.47, 35.05) * mm});
            skLineSegment(sketch, "E919", {"start": v(27.47, 35.05) * mm, "end": v(26.13, 34.62) * mm});
            skLineSegment(sketch, "E920", {"start": v(26.13, 34.62) * mm, "end": v(27.42, 34.05) * mm});
            skLineSegment(sketch, "E921", {"start": v(27.42, 34.05) * mm, "end": v(28.13, 34.52) * mm});
            skLineSegment(sketch, "E922", {"start": v(19.65, 32.23) * mm, "end": v(20.5, 32.19) * mm});
            skLineSegment(sketch, "E923", {"start": v(20.5, 32.19) * mm, "end": v(21.33, 33.32) * mm});
            skLineSegment(sketch, "E924", {"start": v(21.33, 33.32) * mm, "end": v(19.96, 33.02) * mm});
            skLineSegment(sketch, "E925", {"start": v(19.96, 33.02) * mm, "end": v(19.65, 32.23) * mm});
            skSolve(sketch);
        }
        {
            var Q0;
            Q0=qCreatedBy(makeId("Right.planeOp"),FACE);
            var sketch = newSketch(context, id + "F3", { "sketchPlane" : qUnion([Q0])});
            skLineSegment(sketch, "E926", {"start": v(0, -70.92) * mm, "end": v(0, 69.35) * mm, "construction": true});
            skSolve(sketch);
        }
        {
            var Q0;
            Q0=makeQuery(id+"F1.opExtrude","CAP_FACE",FACE,{"disambiguationData":[OSD([sQuery(id+"F0.wireOp",EDGE,"E0.bottom"),sQuery(id+"F0.wireOp",EDGE,"E0.top"),sQuery(id+"F0.wireOp",EDGE,"E0.left"),sQuery(id+"F0.wireOp",EDGE,"E0.right"),sQuery(id+"F0.wireOp",EDGE,"E1"),sQuery(id+"F0.wireOp",EDGE,"E2"),sQuery(id+"F0.wireOp",EDGE,"E3"),sQuery(id+"F0.wireOp",EDGE,"E4.MirrorCS"),sQuery(id+"F0.wireOp",EDGE,"E5.MirrorCS"),sQuery(id+"F0.wireOp",EDGE,"E6.MirrorCS"),sQuery(id+"F0.wireOp",EDGE,"E7.MirrorCS"),sQuery(id+"F0.wireOp",EDGE,"E8.MirrorCS"),sQuery(id+"F0.wireOp",EDGE,"E9.trimOffspring"),sQuery(id+"F0.wireOp",EDGE,"E10.trimOffspring"),sQuery(id+"F0.wireOp",EDGE,"E11.trimOffspring"),sQuery(id+"F0.wireOp",EDGE,"E12.trimOffspring")])],"isStart":false});
            var sketch = newSketch(context, id + "F4", { "sketchPlane" : qUnion([Q0])});
            skLineSegment(sketch, "E927.bottom", {"start": v(-50, 28.2) * mm, "end": v(50, 28.2) * mm});
            skLineSegment(sketch, "E927.top", {"start": v(-50, -36.8) * mm, "end": v(50, -36.8) * mm});
            skLineSegment(sketch, "E927.left", {"start": v(-50, 28.2) * mm, "end": v(-50, -36.8) * mm});
            skLineSegment(sketch, "E927.right", {"start": v(50, 28.2) * mm, "end": v(50, -36.8) * mm});
            skSolve(sketch);
        }
        {
            var Q0;
            Q0=makeQuery(id+"F4.imprint","IMPRINT",FACE,{"disambiguationData":[TD([[makeQuery(id+"F4.imprint","IMPRINT",EDGE,{"derivedFrom":sQuery(id+"F4.wireOp",EDGE,"E927.bottom")}),-1.0]])]});
            extrude(context, id + "F5", {"entities" : qUnion([Q0]), "operationType" : NewBodyOperationType.REMOVE, "oppositeDirection" : true, "depth" : 5 * mm});
        }
        {
            var Q0;
            Q0 = qSketchRegion(id + "F2", true);
            extrude(context, id + "F6", {"entities" : qUnion([Q0]), "operationType" : NewBodyOperationType.ADD, "depth" : 2 * mm});
        }
        {
            var Q0;
            {var subQ0=sQuery(id+"F0.wireOp",EDGE,"E3");var subQ1=sQuery(id+"F0.wireOp",EDGE,"E0.bottom");var subQ2=sQuery(id+"F0.wireOp",EDGE,"E6.MirrorCS");var subQ3=sQuery(id+"F0.wireOp",EDGE,"E7.MirrorCS");var subQ4=sQuery(id+"F0.wireOp",EDGE,"E8.MirrorCS");var subQ5=sQuery(id+"F0.wireOp",EDGE,"E9.trimOffspring");var subQ6=sQuery(id+"F0.wireOp",EDGE,"E10.trimOffspring");var subQ7=sQuery(id+"F0.wireOp",EDGE,"E11.trimOffspring");var subQ8=sQuery(id+"F0.wireOp",EDGE,"E12.trimOffspring");var subQ9=sQuery(id+"F0.wireOp",EDGE,"E0.top");var subQ10=sQuery(id+"F0.wireOp",EDGE,"E0.left");var subQ11=sQuery(id+"F0.wireOp",EDGE,"E0.right");var subQ12=sQuery(id+"F0.wireOp",EDGE,"E1");var subQ13=sQuery(id+"F0.wireOp",EDGE,"E2");var subQ14=sQuery(id+"F0.wireOp",EDGE,"E4.MirrorCS");var subQ15=sQuery(id+"F0.wireOp",EDGE,"E5.MirrorCS");Q0=makeQuery(id+"F6.boolean.opBoolean","SPLIT",FACE,{"disambiguationData":[TD([makeQuery(id+"F1.opExtrude","SWEPT_FACE",FACE,{"disambiguationData":[OSD([subQ1])]})])],"derivedFrom":makeQuery(id+"F1.opExtrude","CAP_FACE",FACE,{"disambiguationData":[OSD([subQ1,subQ9,subQ10,subQ11,subQ12,subQ13,subQ0,subQ14,subQ15,subQ2,subQ3,subQ4,subQ5,subQ6,subQ7,subQ8])],"isStart":false})});}
            var sketch = newSketch(context, id + "F7", { "sketchPlane" : qUnion([Q0])});
            skText(sketch, "E928", { "text": "        I LOVE YOU GG!\nMERRY CHRISTMAS - 2016", "fontName": "OpenSans-BoldItalic.ttf"});
            const initialGuessF7  = {"E928": [-0.045, -0.04373, 1, 0, 0.00543]};
            skSetInitialGuess(sketch, initialGuessF7);
            skSolve(sketch);
        }
        {
            var Q0;
            Q0 = qSketchRegion(id + "F7", true);
            extrude(context, id + "F8", {"entities" : qUnion([Q0]), "operationType" : NewBodyOperationType.ADD, "depth" : 2 * mm});
        }
    });
